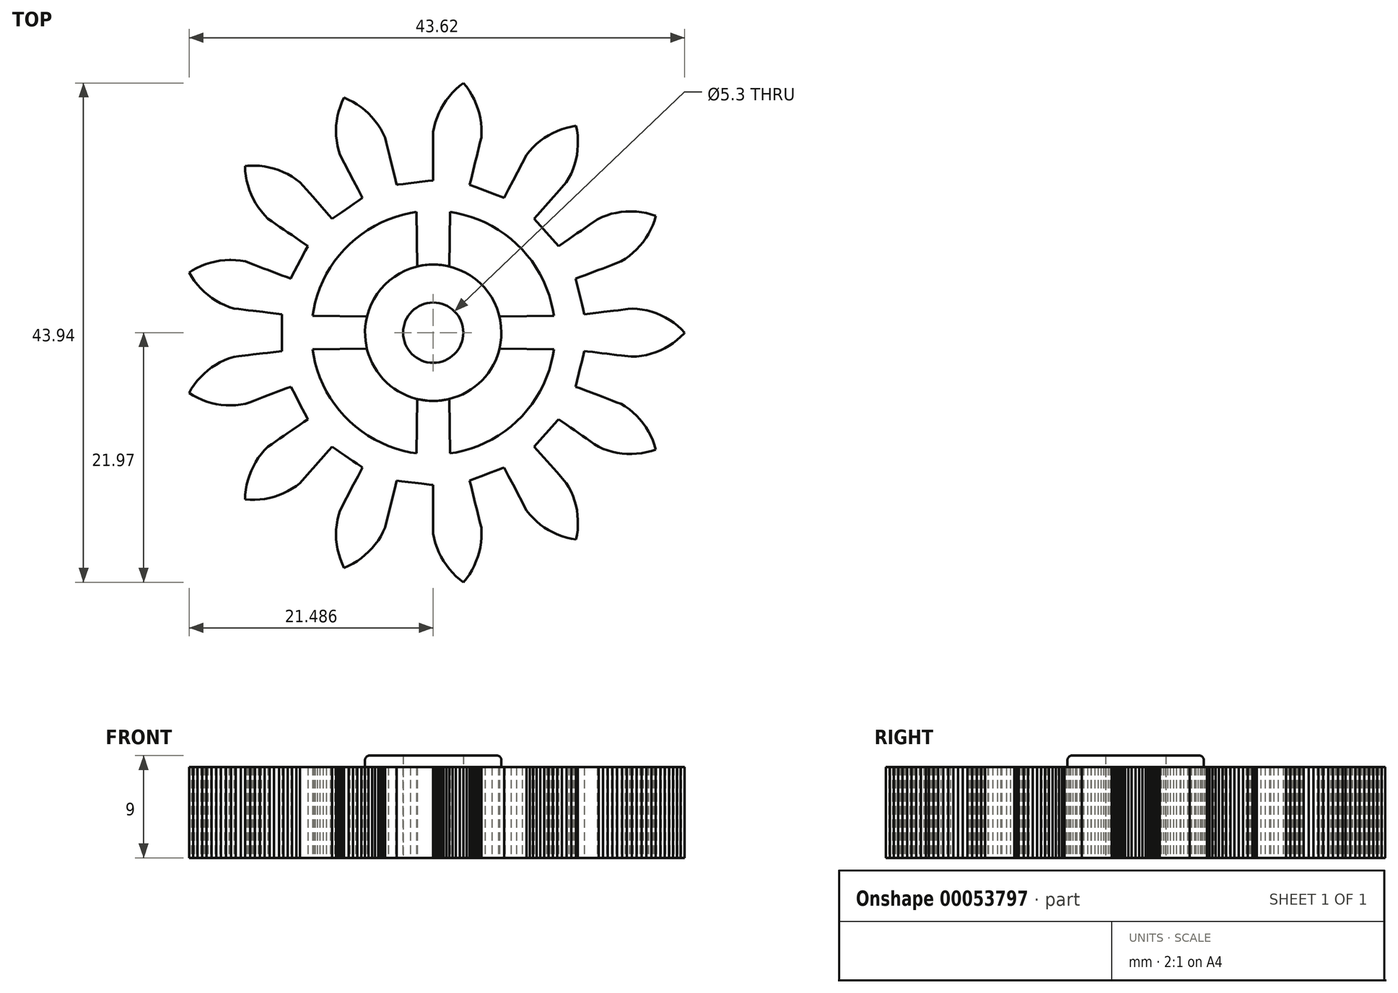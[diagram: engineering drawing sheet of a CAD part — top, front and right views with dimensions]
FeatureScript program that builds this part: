
annotation { "Feature Type Name" : "Feature", "Feature Type Description" : "" }
export const myFeature = defineFeature(function(context is Context, id is Id, definition is map)
    precondition{}
    {
        {
            var Q0;
            Q0=qCreatedBy(makeId("Top.planeOp"),FACE);
            var sketch = newSketch(context, id + "F0", { "sketchPlane" : qUnion([Q0])});
            skLineSegment(sketch, "E0", {"start": v(10.41, -1.62) * mm, "end": v(10.7, -1.65) * mm});
            skLineSegment(sketch, "E1", {"start": v(10.7, -1.65) * mm, "end": v(11.12, -1.7) * mm});
            skLineSegment(sketch, "E2", {"start": v(11.12, -1.7) * mm, "end": v(11.54, -1.75) * mm});
            skLineSegment(sketch, "E3", {"start": v(11.54, -1.75) * mm, "end": v(11.97, -1.8) * mm});
            skLineSegment(sketch, "E4", {"start": v(11.97, -1.8) * mm, "end": v(12.4, -1.86) * mm});
            skLineSegment(sketch, "E5", {"start": v(12.4, -1.86) * mm, "end": v(12.82, -1.9) * mm});
            skLineSegment(sketch, "E6", {"start": v(12.82, -1.9) * mm, "end": v(13.24, -1.96) * mm});
            skLineSegment(sketch, "E7", {"start": v(13.24, -1.96) * mm, "end": v(13.67, -2.01) * mm});
            skLineSegment(sketch, "E8", {"start": v(13.67, -2.01) * mm, "end": v(14.09, -2.06) * mm});
            skLineSegment(sketch, "E9", {"start": v(14.09, -2.06) * mm, "end": v(14.51, -2.11) * mm});
            skLineSegment(sketch, "E10", {"start": v(14.51, -2.11) * mm, "end": v(15, -2.1) * mm});
            skLineSegment(sketch, "E11", {"start": v(15, -2.1) * mm, "end": v(15.44, -2.05) * mm});
            skLineSegment(sketch, "E12", {"start": v(15.44, -2.05) * mm, "end": v(15.85, -1.97) * mm});
            skLineSegment(sketch, "E13", {"start": v(15.85, -1.97) * mm, "end": v(16.28, -1.86) * mm});
            skLineSegment(sketch, "E14", {"start": v(16.28, -1.86) * mm, "end": v(16.68, -1.72) * mm});
            skLineSegment(sketch, "E15", {"start": v(16.68, -1.72) * mm, "end": v(17.09, -1.55) * mm});
            skLineSegment(sketch, "E16", {"start": v(17.09, -1.55) * mm, "end": v(17.47, -1.37) * mm});
            skLineSegment(sketch, "E17", {"start": v(17.47, -1.37) * mm, "end": v(17.85, -1.15) * mm});
            skLineSegment(sketch, "E18", {"start": v(17.85, -1.15) * mm, "end": v(18.2, -0.92) * mm});
            skLineSegment(sketch, "E19", {"start": v(18.2, -0.92) * mm, "end": v(18.55, -0.64) * mm});
            skLineSegment(sketch, "E20", {"start": v(18.55, -0.64) * mm, "end": v(18.87, -0.37) * mm});
            skLineSegment(sketch, "E21", {"start": v(18.87, -0.37) * mm, "end": v(19.18, -0.05) * mm});
            skLineSegment(sketch, "E22", {"start": v(19.18, -0.05) * mm, "end": v(19.24, 0) * mm});
            skLineSegment(sketch, "E23", {"start": v(19.24, 0) * mm, "end": v(18.92, 0.31) * mm});
            skLineSegment(sketch, "E24", {"start": v(18.92, 0.31) * mm, "end": v(18.61, 0.6) * mm});
            skLineSegment(sketch, "E25", {"start": v(18.61, 0.6) * mm, "end": v(18.26, 0.87) * mm});
            skLineSegment(sketch, "E26", {"start": v(18.26, 0.87) * mm, "end": v(17.92, 1.1) * mm});
            skLineSegment(sketch, "E27", {"start": v(17.92, 1.1) * mm, "end": v(17.53, 1.33) * mm});
            skLineSegment(sketch, "E28", {"start": v(17.53, 1.33) * mm, "end": v(17.16, 1.52) * mm});
            skLineSegment(sketch, "E29", {"start": v(17.16, 1.52) * mm, "end": v(16.75, 1.7) * mm});
            skLineSegment(sketch, "E30", {"start": v(16.75, 1.7) * mm, "end": v(16.35, 1.84) * mm});
            skLineSegment(sketch, "E31", {"start": v(16.35, 1.84) * mm, "end": v(15.93, 1.95) * mm});
            skLineSegment(sketch, "E32", {"start": v(15.93, 1.95) * mm, "end": v(15.51, 2.04) * mm});
            skLineSegment(sketch, "E33", {"start": v(15.51, 2.04) * mm, "end": v(15.07, 2.1) * mm});
            skLineSegment(sketch, "E34", {"start": v(15.07, 2.1) * mm, "end": v(14.65, 2.13) * mm});
            skLineSegment(sketch, "E35", {"start": v(14.65, 2.13) * mm, "end": v(14.23, 2.08) * mm});
            skLineSegment(sketch, "E36", {"start": v(14.23, 2.08) * mm, "end": v(13.8, 2.03) * mm});
            skLineSegment(sketch, "E37", {"start": v(13.8, 2.03) * mm, "end": v(13.38, 1.98) * mm});
            skLineSegment(sketch, "E38", {"start": v(13.38, 1.98) * mm, "end": v(12.96, 1.92) * mm});
            skLineSegment(sketch, "E39", {"start": v(12.96, 1.92) * mm, "end": v(12.53, 1.87) * mm});
            skLineSegment(sketch, "E40", {"start": v(12.53, 1.87) * mm, "end": v(12.11, 1.82) * mm});
            skLineSegment(sketch, "E41", {"start": v(12.11, 1.82) * mm, "end": v(11.69, 1.77) * mm});
            skLineSegment(sketch, "E42", {"start": v(11.69, 1.77) * mm, "end": v(11.26, 1.72) * mm});
            skLineSegment(sketch, "E43", {"start": v(11.26, 1.72) * mm, "end": v(10.84, 1.67) * mm});
            skLineSegment(sketch, "E44", {"start": v(10.84, 1.67) * mm, "end": v(10.41, 1.62) * mm});
            skLineSegment(sketch, "E45", {"start": v(10.41, 1.62) * mm, "end": v(10.3, 2.05) * mm});
            skLineSegment(sketch, "E46", {"start": v(10.3, 2.05) * mm, "end": v(10.2, 2.48) * mm});
            skLineSegment(sketch, "E47", {"start": v(10.2, 2.48) * mm, "end": v(10.1, 2.9) * mm});
            skLineSegment(sketch, "E48", {"start": v(10.1, 2.9) * mm, "end": v(9.99, 3.34) * mm});
            skLineSegment(sketch, "E49", {"start": v(9.99, 3.34) * mm, "end": v(9.88, 3.77) * mm});
            skLineSegment(sketch, "E50", {"start": v(9.88, 3.77) * mm, "end": v(9.78, 4.2) * mm});
            skLineSegment(sketch, "E51", {"start": v(9.78, 4.2) * mm, "end": v(9.67, 4.63) * mm});
            skLineSegment(sketch, "E52", {"start": v(9.67, 4.63) * mm, "end": v(9.64, 4.75) * mm});
            skLineSegment(sketch, "E53", {"start": v(9.64, 4.75) * mm, "end": v(10.04, 4.9) * mm});
            skLineSegment(sketch, "E54", {"start": v(10.04, 4.9) * mm, "end": v(10.44, 5.06) * mm});
            skLineSegment(sketch, "E55", {"start": v(10.44, 5.06) * mm, "end": v(10.84, 5.2) * mm});
            skLineSegment(sketch, "E56", {"start": v(10.84, 5.2) * mm, "end": v(11.24, 5.36) * mm});
            skLineSegment(sketch, "E57", {"start": v(11.24, 5.36) * mm, "end": v(11.64, 5.51) * mm});
            skLineSegment(sketch, "E58", {"start": v(11.64, 5.51) * mm, "end": v(12.04, 5.66) * mm});
            skLineSegment(sketch, "E59", {"start": v(12.04, 5.66) * mm, "end": v(12.44, 5.81) * mm});
            skLineSegment(sketch, "E60", {"start": v(12.44, 5.81) * mm, "end": v(12.84, 5.97) * mm});
            skLineSegment(sketch, "E61", {"start": v(12.84, 5.97) * mm, "end": v(13.24, 6.12) * mm});
            skLineSegment(sketch, "E62", {"start": v(13.24, 6.12) * mm, "end": v(13.63, 6.27) * mm});
            skLineSegment(sketch, "E63", {"start": v(13.63, 6.27) * mm, "end": v(14, 6.5) * mm});
            skLineSegment(sketch, "E64", {"start": v(14, 6.5) * mm, "end": v(14.35, 6.75) * mm});
            skLineSegment(sketch, "E65", {"start": v(14.35, 6.75) * mm, "end": v(14.7, 7.03) * mm});
            skLineSegment(sketch, "E66", {"start": v(14.7, 7.03) * mm, "end": v(15, 7.32) * mm});
            skLineSegment(sketch, "E67", {"start": v(15, 7.32) * mm, "end": v(15.3, 7.64) * mm});
            skLineSegment(sketch, "E68", {"start": v(15.3, 7.64) * mm, "end": v(15.57, 7.97) * mm});
            skLineSegment(sketch, "E69", {"start": v(15.57, 7.97) * mm, "end": v(15.82, 8.33) * mm});
            skLineSegment(sketch, "E70", {"start": v(15.82, 8.33) * mm, "end": v(16.05, 8.69) * mm});
            skLineSegment(sketch, "E71", {"start": v(16.05, 8.69) * mm, "end": v(16.25, 9.08) * mm});
            skLineSegment(sketch, "E72", {"start": v(16.25, 9.08) * mm, "end": v(16.43, 9.46) * mm});
            skLineSegment(sketch, "E73", {"start": v(16.43, 9.46) * mm, "end": v(16.58, 9.88) * mm});
            skLineSegment(sketch, "E74", {"start": v(16.58, 9.88) * mm, "end": v(16.7, 10.28) * mm});
            skLineSegment(sketch, "E75", {"start": v(16.7, 10.28) * mm, "end": v(16.28, 10.42) * mm});
            skLineSegment(sketch, "E76", {"start": v(16.28, 10.42) * mm, "end": v(15.87, 10.52) * mm});
            skLineSegment(sketch, "E77", {"start": v(15.87, 10.52) * mm, "end": v(15.43, 10.6) * mm});
            skLineSegment(sketch, "E78", {"start": v(15.43, 10.6) * mm, "end": v(15.02, 10.65) * mm});
            skLineSegment(sketch, "E79", {"start": v(15.02, 10.65) * mm, "end": v(14.57, 10.67) * mm});
            skLineSegment(sketch, "E80", {"start": v(14.57, 10.67) * mm, "end": v(14.5, 10.68) * mm});
            skLineSegment(sketch, "E81", {"start": v(14.5, 10.68) * mm, "end": v(14.06, 10.66) * mm});
            skLineSegment(sketch, "E82", {"start": v(14.06, 10.66) * mm, "end": v(13.64, 10.62) * mm});
            skLineSegment(sketch, "E83", {"start": v(13.64, 10.62) * mm, "end": v(13.2, 10.55) * mm});
            skLineSegment(sketch, "E84", {"start": v(13.2, 10.55) * mm, "end": v(12.79, 10.46) * mm});
            skLineSegment(sketch, "E85", {"start": v(12.79, 10.46) * mm, "end": v(12.37, 10.33) * mm});
            skLineSegment(sketch, "E86", {"start": v(12.37, 10.33) * mm, "end": v(11.97, 10.18) * mm});
            skLineSegment(sketch, "E87", {"start": v(11.97, 10.18) * mm, "end": v(11.54, 9.96) * mm});
            skLineSegment(sketch, "E88", {"start": v(11.54, 9.96) * mm, "end": v(11.19, 9.72) * mm});
            skLineSegment(sketch, "E89", {"start": v(11.19, 9.72) * mm, "end": v(10.83, 9.48) * mm});
            skLineSegment(sketch, "E90", {"start": v(10.83, 9.48) * mm, "end": v(10.48, 9.23) * mm});
            skLineSegment(sketch, "E91", {"start": v(10.48, 9.23) * mm, "end": v(10.13, 9) * mm});
            skLineSegment(sketch, "E92", {"start": v(10.13, 9) * mm, "end": v(9.78, 8.75) * mm});
            skLineSegment(sketch, "E93", {"start": v(9.78, 8.75) * mm, "end": v(9.43, 8.5) * mm});
            skLineSegment(sketch, "E94", {"start": v(9.43, 8.5) * mm, "end": v(9.08, 8.26) * mm});
            skLineSegment(sketch, "E95", {"start": v(9.08, 8.26) * mm, "end": v(8.72, 8.02) * mm});
            skLineSegment(sketch, "E96", {"start": v(8.72, 8.02) * mm, "end": v(8.37, 7.78) * mm});
            skLineSegment(sketch, "E97", {"start": v(8.37, 7.78) * mm, "end": v(8.14, 7.62) * mm});
            skLineSegment(sketch, "E98", {"start": v(8.14, 7.62) * mm, "end": v(7.84, 7.95) * mm});
            skLineSegment(sketch, "E99", {"start": v(7.84, 7.95) * mm, "end": v(7.55, 8.28) * mm});
            skLineSegment(sketch, "E100", {"start": v(7.55, 8.28) * mm, "end": v(7.26, 8.6) * mm});
            skLineSegment(sketch, "E101", {"start": v(7.26, 8.6) * mm, "end": v(6.96, 8.94) * mm});
            skLineSegment(sketch, "E102", {"start": v(6.96, 8.94) * mm, "end": v(6.67, 9.27) * mm});
            skLineSegment(sketch, "E103", {"start": v(6.67, 9.27) * mm, "end": v(6.38, 9.6) * mm});
            skLineSegment(sketch, "E104", {"start": v(6.38, 9.6) * mm, "end": v(6.08, 9.94) * mm});
            skLineSegment(sketch, "E105", {"start": v(6.08, 9.94) * mm, "end": v(6, 10.03) * mm});
            skLineSegment(sketch, "E106", {"start": v(6, 10.03) * mm, "end": v(6.28, 10.35) * mm});
            skLineSegment(sketch, "E107", {"start": v(6.28, 10.35) * mm, "end": v(6.56, 10.67) * mm});
            skLineSegment(sketch, "E108", {"start": v(6.56, 10.67) * mm, "end": v(6.85, 11) * mm});
            skLineSegment(sketch, "E109", {"start": v(6.85, 11) * mm, "end": v(7.13, 11.31) * mm});
            skLineSegment(sketch, "E110", {"start": v(7.13, 11.31) * mm, "end": v(7.41, 11.63) * mm});
            skLineSegment(sketch, "E111", {"start": v(7.41, 11.63) * mm, "end": v(7.7, 11.95) * mm});
            skLineSegment(sketch, "E112", {"start": v(7.7, 11.95) * mm, "end": v(7.98, 12.27) * mm});
            skLineSegment(sketch, "E113", {"start": v(7.98, 12.27) * mm, "end": v(8.26, 12.6) * mm});
            skLineSegment(sketch, "E114", {"start": v(8.26, 12.6) * mm, "end": v(8.55, 12.91) * mm});
            skLineSegment(sketch, "E115", {"start": v(8.55, 12.91) * mm, "end": v(8.83, 13.23) * mm});
            skLineSegment(sketch, "E116", {"start": v(8.83, 13.23) * mm, "end": v(9.05, 13.62) * mm});
            skLineSegment(sketch, "E117", {"start": v(9.05, 13.62) * mm, "end": v(9.24, 14) * mm});
            skLineSegment(sketch, "E118", {"start": v(9.24, 14) * mm, "end": v(9.41, 14.4) * mm});
            skLineSegment(sketch, "E119", {"start": v(9.41, 14.4) * mm, "end": v(9.55, 14.8) * mm});
            skLineSegment(sketch, "E120", {"start": v(9.55, 14.8) * mm, "end": v(9.66, 15.23) * mm});
            skLineSegment(sketch, "E121", {"start": v(9.66, 15.23) * mm, "end": v(9.75, 15.64) * mm});
            skLineSegment(sketch, "E122", {"start": v(9.75, 15.64) * mm, "end": v(9.8, 16.08) * mm});
            skLineSegment(sketch, "E123", {"start": v(9.8, 16.08) * mm, "end": v(9.84, 16.5) * mm});
            skLineSegment(sketch, "E124", {"start": v(9.84, 16.5) * mm, "end": v(9.84, 16.94) * mm});
            skLineSegment(sketch, "E125", {"start": v(9.84, 16.94) * mm, "end": v(9.82, 17.36) * mm});
            skLineSegment(sketch, "E126", {"start": v(9.82, 17.36) * mm, "end": v(9.76, 17.8) * mm});
            skLineSegment(sketch, "E127", {"start": v(9.76, 17.8) * mm, "end": v(9.68, 18.21) * mm});
            skLineSegment(sketch, "E128", {"start": v(9.68, 18.21) * mm, "end": v(9.24, 18.13) * mm});
            skLineSegment(sketch, "E129", {"start": v(9.24, 18.13) * mm, "end": v(8.83, 18.04) * mm});
            skLineSegment(sketch, "E130", {"start": v(8.83, 18.04) * mm, "end": v(8.4, 17.9) * mm});
            skLineSegment(sketch, "E131", {"start": v(8.4, 17.9) * mm, "end": v(8.01, 17.76) * mm});
            skLineSegment(sketch, "E132", {"start": v(8.01, 17.76) * mm, "end": v(7.61, 17.57) * mm});
            skLineSegment(sketch, "E133", {"start": v(7.61, 17.57) * mm, "end": v(7.24, 17.37) * mm});
            skLineSegment(sketch, "E134", {"start": v(7.24, 17.37) * mm, "end": v(6.87, 17.13) * mm});
            skLineSegment(sketch, "E135", {"start": v(6.87, 17.13) * mm, "end": v(6.53, 16.88) * mm});
            skLineSegment(sketch, "E136", {"start": v(6.53, 16.88) * mm, "end": v(6.2, 16.6) * mm});
            skLineSegment(sketch, "E137", {"start": v(6.2, 16.6) * mm, "end": v(5.88, 16.3) * mm});
            skLineSegment(sketch, "E138", {"start": v(5.88, 16.3) * mm, "end": v(5.59, 15.98) * mm});
            skLineSegment(sketch, "E139", {"start": v(5.59, 15.98) * mm, "end": v(5.32, 15.65) * mm});
            skLineSegment(sketch, "E140", {"start": v(5.32, 15.65) * mm, "end": v(5.12, 15.27) * mm});
            skLineSegment(sketch, "E141", {"start": v(5.12, 15.27) * mm, "end": v(4.92, 14.9) * mm});
            skLineSegment(sketch, "E142", {"start": v(4.92, 14.9) * mm, "end": v(4.73, 14.52) * mm});
            skLineSegment(sketch, "E143", {"start": v(4.73, 14.52) * mm, "end": v(4.53, 14.14) * mm});
            skLineSegment(sketch, "E144", {"start": v(4.53, 14.14) * mm, "end": v(4.33, 13.76) * mm});
            skLineSegment(sketch, "E145", {"start": v(4.33, 13.76) * mm, "end": v(4.13, 13.38) * mm});
            skLineSegment(sketch, "E146", {"start": v(4.13, 13.38) * mm, "end": v(3.93, 13) * mm});
            skLineSegment(sketch, "E147", {"start": v(3.93, 13) * mm, "end": v(3.73, 12.63) * mm});
            skLineSegment(sketch, "E148", {"start": v(3.73, 12.63) * mm, "end": v(3.53, 12.25) * mm});
            skLineSegment(sketch, "E149", {"start": v(3.53, 12.25) * mm, "end": v(3.34, 11.87) * mm});
            skLineSegment(sketch, "E150", {"start": v(3.34, 11.87) * mm, "end": v(2.92, 12.03) * mm});
            skLineSegment(sketch, "E151", {"start": v(2.92, 12.03) * mm, "end": v(2.5, 12.18) * mm});
            skLineSegment(sketch, "E152", {"start": v(2.5, 12.18) * mm, "end": v(2.1, 12.34) * mm});
            skLineSegment(sketch, "E153", {"start": v(2.1, 12.34) * mm, "end": v(1.68, 12.5) * mm});
            skLineSegment(sketch, "E154", {"start": v(1.68, 12.5) * mm, "end": v(1.26, 12.66) * mm});
            skLineSegment(sketch, "E155", {"start": v(1.26, 12.66) * mm, "end": v(0.85, 12.81) * mm});
            skLineSegment(sketch, "E156", {"start": v(0.85, 12.81) * mm, "end": v(0.44, 12.97) * mm});
            skLineSegment(sketch, "E157", {"start": v(0.44, 12.97) * mm, "end": v(0.31, 13.02) * mm});
            skLineSegment(sketch, "E158", {"start": v(0.31, 13.02) * mm, "end": v(0.42, 13.43) * mm});
            skLineSegment(sketch, "E159", {"start": v(0.42, 13.43) * mm, "end": v(0.52, 13.85) * mm});
            skLineSegment(sketch, "E160", {"start": v(0.52, 13.85) * mm, "end": v(0.62, 14.26) * mm});
            skLineSegment(sketch, "E161", {"start": v(0.62, 14.26) * mm, "end": v(0.72, 14.68) * mm});
            skLineSegment(sketch, "E162", {"start": v(0.72, 14.68) * mm, "end": v(0.83, 15.1) * mm});
            skLineSegment(sketch, "E163", {"start": v(0.83, 15.1) * mm, "end": v(0.93, 15.5) * mm});
            skLineSegment(sketch, "E164", {"start": v(0.93, 15.5) * mm, "end": v(1.03, 15.92) * mm});
            skLineSegment(sketch, "E165", {"start": v(1.03, 15.92) * mm, "end": v(1.13, 16.33) * mm});
            skLineSegment(sketch, "E166", {"start": v(1.13, 16.33) * mm, "end": v(1.23, 16.75) * mm});
            skLineSegment(sketch, "E167", {"start": v(1.23, 16.75) * mm, "end": v(1.34, 17.16) * mm});
            skLineSegment(sketch, "E168", {"start": v(1.34, 17.16) * mm, "end": v(1.35, 17.6) * mm});
            skLineSegment(sketch, "E169", {"start": v(1.35, 17.6) * mm, "end": v(1.35, 18.03) * mm});
            skLineSegment(sketch, "E170", {"start": v(1.35, 18.03) * mm, "end": v(1.3, 18.47) * mm});
            skLineSegment(sketch, "E171", {"start": v(1.3, 18.47) * mm, "end": v(1.25, 18.89) * mm});
            skLineSegment(sketch, "E172", {"start": v(1.25, 18.89) * mm, "end": v(1.15, 19.32) * mm});
            skLineSegment(sketch, "E173", {"start": v(1.15, 19.32) * mm, "end": v(1.04, 19.72) * mm});
            skLineSegment(sketch, "E174", {"start": v(1.04, 19.72) * mm, "end": v(0.88, 20.14) * mm});
            skLineSegment(sketch, "E175", {"start": v(0.88, 20.14) * mm, "end": v(0.72, 20.52) * mm});
            skLineSegment(sketch, "E176", {"start": v(0.72, 20.52) * mm, "end": v(0.5, 20.92) * mm});
            skLineSegment(sketch, "E177", {"start": v(0.5, 20.92) * mm, "end": v(0.3, 21.28) * mm});
            skLineSegment(sketch, "E178", {"start": v(0.3, 21.28) * mm, "end": v(0.04, 21.64) * mm});
            skLineSegment(sketch, "E179", {"start": v(0.04, 21.64) * mm, "end": v(-0.23, 21.97) * mm});
            skLineSegment(sketch, "E180", {"start": v(-0.23, 21.97) * mm, "end": v(-0.58, 21.7) * mm});
            skLineSegment(sketch, "E181", {"start": v(-0.58, 21.7) * mm, "end": v(-0.9, 21.42) * mm});
            skLineSegment(sketch, "E182", {"start": v(-0.9, 21.42) * mm, "end": v(-1.2, 21.1) * mm});
            skLineSegment(sketch, "E183", {"start": v(-1.2, 21.1) * mm, "end": v(-1.49, 20.8) * mm});
            skLineSegment(sketch, "E184", {"start": v(-1.49, 20.8) * mm, "end": v(-1.75, 20.44) * mm});
            skLineSegment(sketch, "E185", {"start": v(-1.75, 20.44) * mm, "end": v(-1.99, 20.1) * mm});
            skLineSegment(sketch, "E186", {"start": v(-1.99, 20.1) * mm, "end": v(-2.2, 19.7) * mm});
            skLineSegment(sketch, "E187", {"start": v(-2.2, 19.7) * mm, "end": v(-2.4, 19.33) * mm});
            skLineSegment(sketch, "E188", {"start": v(-2.4, 19.33) * mm, "end": v(-2.56, 18.92) * mm});
            skLineSegment(sketch, "E189", {"start": v(-2.56, 18.92) * mm, "end": v(-2.7, 18.52) * mm});
            skLineSegment(sketch, "E190", {"start": v(-2.7, 18.52) * mm, "end": v(-2.81, 18.1) * mm});
            skLineSegment(sketch, "E191", {"start": v(-2.81, 18.1) * mm, "end": v(-2.9, 17.68) * mm});
            skLineSegment(sketch, "E192", {"start": v(-2.9, 17.68) * mm, "end": v(-2.9, 17.25) * mm});
            skLineSegment(sketch, "E193", {"start": v(-2.9, 17.25) * mm, "end": v(-2.9, 16.82) * mm});
            skLineSegment(sketch, "E194", {"start": v(-2.9, 16.82) * mm, "end": v(-2.9, 16.4) * mm});
            skLineSegment(sketch, "E195", {"start": v(-2.9, 16.4) * mm, "end": v(-2.9, 15.97) * mm});
            skLineSegment(sketch, "E196", {"start": v(-2.9, 15.97) * mm, "end": v(-2.9, 15.54) * mm});
            skLineSegment(sketch, "E197", {"start": v(-2.9, 15.54) * mm, "end": v(-2.9, 15.11) * mm});
            skLineSegment(sketch, "E198", {"start": v(-2.9, 15.11) * mm, "end": v(-2.9, 14.69) * mm});
            skLineSegment(sketch, "E199", {"start": v(-2.9, 14.69) * mm, "end": v(-2.9, 14.26) * mm});
            skLineSegment(sketch, "E200", {"start": v(-2.9, 14.26) * mm, "end": v(-2.9, 13.83) * mm});
            skLineSegment(sketch, "E201", {"start": v(-2.9, 13.83) * mm, "end": v(-2.9, 13.4) * mm});
            skLineSegment(sketch, "E202", {"start": v(-2.9, 13.4) * mm, "end": v(-3.33, 13.35) * mm});
            skLineSegment(sketch, "E203", {"start": v(-3.33, 13.35) * mm, "end": v(-3.77, 13.3) * mm});
            skLineSegment(sketch, "E204", {"start": v(-3.77, 13.3) * mm, "end": v(-4.21, 13.25) * mm});
            skLineSegment(sketch, "E205", {"start": v(-4.21, 13.25) * mm, "end": v(-4.65, 13.2) * mm});
            skLineSegment(sketch, "E206", {"start": v(-4.65, 13.2) * mm, "end": v(-5.1, 13.14) * mm});
            skLineSegment(sketch, "E207", {"start": v(-5.1, 13.14) * mm, "end": v(-5.53, 13.09) * mm});
            skLineSegment(sketch, "E208", {"start": v(-5.53, 13.09) * mm, "end": v(-5.97, 13.03) * mm});
            skLineSegment(sketch, "E209", {"start": v(-5.97, 13.03) * mm, "end": v(-6.1, 13.02) * mm});
            skLineSegment(sketch, "E210", {"start": v(-6.1, 13.02) * mm, "end": v(-6.2, 13.43) * mm});
            skLineSegment(sketch, "E211", {"start": v(-6.2, 13.43) * mm, "end": v(-6.3, 13.85) * mm});
            skLineSegment(sketch, "E212", {"start": v(-6.3, 13.85) * mm, "end": v(-6.4, 14.26) * mm});
            skLineSegment(sketch, "E213", {"start": v(-6.4, 14.26) * mm, "end": v(-6.51, 14.68) * mm});
            skLineSegment(sketch, "E214", {"start": v(-6.51, 14.68) * mm, "end": v(-6.61, 15.1) * mm});
            skLineSegment(sketch, "E215", {"start": v(-6.61, 15.1) * mm, "end": v(-6.72, 15.5) * mm});
            skLineSegment(sketch, "E216", {"start": v(-6.72, 15.5) * mm, "end": v(-6.82, 15.92) * mm});
            skLineSegment(sketch, "E217", {"start": v(-6.82, 15.92) * mm, "end": v(-6.92, 16.33) * mm});
            skLineSegment(sketch, "E218", {"start": v(-6.92, 16.33) * mm, "end": v(-7.02, 16.75) * mm});
            skLineSegment(sketch, "E219", {"start": v(-7.02, 16.75) * mm, "end": v(-7.12, 17.16) * mm});
            skLineSegment(sketch, "E220", {"start": v(-7.12, 17.16) * mm, "end": v(-7.31, 17.56) * mm});
            skLineSegment(sketch, "E221", {"start": v(-7.31, 17.56) * mm, "end": v(-7.51, 17.93) * mm});
            skLineSegment(sketch, "E222", {"start": v(-7.51, 17.93) * mm, "end": v(-7.76, 18.3) * mm});
            skLineSegment(sketch, "E223", {"start": v(-7.76, 18.3) * mm, "end": v(-8, 18.65) * mm});
            skLineSegment(sketch, "E224", {"start": v(-8, 18.65) * mm, "end": v(-8.29, 18.98) * mm});
            skLineSegment(sketch, "E225", {"start": v(-8.29, 18.98) * mm, "end": v(-8.58, 19.29) * mm});
            skLineSegment(sketch, "E226", {"start": v(-8.58, 19.29) * mm, "end": v(-8.9, 19.59) * mm});
            skLineSegment(sketch, "E227", {"start": v(-8.9, 19.59) * mm, "end": v(-9.24, 19.85) * mm});
            skLineSegment(sketch, "E228", {"start": v(-9.24, 19.85) * mm, "end": v(-9.6, 20.1) * mm});
            skLineSegment(sketch, "E229", {"start": v(-9.6, 20.1) * mm, "end": v(-9.96, 20.32) * mm});
            skLineSegment(sketch, "E230", {"start": v(-9.96, 20.32) * mm, "end": v(-10.36, 20.52) * mm});
            skLineSegment(sketch, "E231", {"start": v(-10.36, 20.52) * mm, "end": v(-10.74, 20.7) * mm});
            skLineSegment(sketch, "E232", {"start": v(-10.74, 20.7) * mm, "end": v(-10.93, 20.29) * mm});
            skLineSegment(sketch, "E233", {"start": v(-10.93, 20.29) * mm, "end": v(-11.08, 19.9) * mm});
            skLineSegment(sketch, "E234", {"start": v(-11.08, 19.9) * mm, "end": v(-11.2, 19.47) * mm});
            skLineSegment(sketch, "E235", {"start": v(-11.2, 19.47) * mm, "end": v(-11.31, 19.06) * mm});
            skLineSegment(sketch, "E236", {"start": v(-11.31, 19.06) * mm, "end": v(-11.38, 18.63) * mm});
            skLineSegment(sketch, "E237", {"start": v(-11.38, 18.63) * mm, "end": v(-11.43, 18.2) * mm});
            skLineSegment(sketch, "E238", {"start": v(-11.43, 18.2) * mm, "end": v(-11.44, 17.77) * mm});
            skLineSegment(sketch, "E239", {"start": v(-11.44, 17.77) * mm, "end": v(-11.44, 17.35) * mm});
            skLineSegment(sketch, "E240", {"start": v(-11.44, 17.35) * mm, "end": v(-11.4, 16.9) * mm});
            skLineSegment(sketch, "E241", {"start": v(-11.4, 16.9) * mm, "end": v(-11.33, 16.49) * mm});
            skLineSegment(sketch, "E242", {"start": v(-11.33, 16.49) * mm, "end": v(-11.23, 16.06) * mm});
            skLineSegment(sketch, "E243", {"start": v(-11.23, 16.06) * mm, "end": v(-11.1, 15.65) * mm});
            skLineSegment(sketch, "E244", {"start": v(-11.1, 15.65) * mm, "end": v(-10.91, 15.27) * mm});
            skLineSegment(sketch, "E245", {"start": v(-10.91, 15.27) * mm, "end": v(-10.71, 14.9) * mm});
            skLineSegment(sketch, "E246", {"start": v(-10.71, 14.9) * mm, "end": v(-10.51, 14.52) * mm});
            skLineSegment(sketch, "E247", {"start": v(-10.51, 14.52) * mm, "end": v(-10.32, 14.14) * mm});
            skLineSegment(sketch, "E248", {"start": v(-10.32, 14.14) * mm, "end": v(-10.12, 13.76) * mm});
            skLineSegment(sketch, "E249", {"start": v(-10.12, 13.76) * mm, "end": v(-9.92, 13.38) * mm});
            skLineSegment(sketch, "E250", {"start": v(-9.92, 13.38) * mm, "end": v(-9.72, 13) * mm});
            skLineSegment(sketch, "E251", {"start": v(-9.72, 13) * mm, "end": v(-9.52, 12.63) * mm});
            skLineSegment(sketch, "E252", {"start": v(-9.52, 12.63) * mm, "end": v(-9.32, 12.25) * mm});
            skLineSegment(sketch, "E253", {"start": v(-9.32, 12.25) * mm, "end": v(-9.12, 11.87) * mm});
            skLineSegment(sketch, "E254", {"start": v(-9.12, 11.87) * mm, "end": v(-9.49, 11.62) * mm});
            skLineSegment(sketch, "E255", {"start": v(-9.49, 11.62) * mm, "end": v(-9.85, 11.37) * mm});
            skLineSegment(sketch, "E256", {"start": v(-9.85, 11.37) * mm, "end": v(-10.22, 11.12) * mm});
            skLineSegment(sketch, "E257", {"start": v(-10.22, 11.12) * mm, "end": v(-10.58, 10.86) * mm});
            skLineSegment(sketch, "E258", {"start": v(-10.58, 10.86) * mm, "end": v(-10.95, 10.61) * mm});
            skLineSegment(sketch, "E259", {"start": v(-10.95, 10.61) * mm, "end": v(-11.31, 10.36) * mm});
            skLineSegment(sketch, "E260", {"start": v(-11.31, 10.36) * mm, "end": v(-11.68, 10.1) * mm});
            skLineSegment(sketch, "E261", {"start": v(-11.68, 10.1) * mm, "end": v(-11.78, 10.03) * mm});
            skLineSegment(sketch, "E262", {"start": v(-11.78, 10.03) * mm, "end": v(-12.07, 10.35) * mm});
            skLineSegment(sketch, "E263", {"start": v(-12.07, 10.35) * mm, "end": v(-12.35, 10.67) * mm});
            skLineSegment(sketch, "E264", {"start": v(-12.35, 10.67) * mm, "end": v(-12.63, 11) * mm});
            skLineSegment(sketch, "E265", {"start": v(-12.63, 11) * mm, "end": v(-12.92, 11.31) * mm});
            skLineSegment(sketch, "E266", {"start": v(-12.92, 11.31) * mm, "end": v(-13.2, 11.63) * mm});
            skLineSegment(sketch, "E267", {"start": v(-13.2, 11.63) * mm, "end": v(-13.48, 11.95) * mm});
            skLineSegment(sketch, "E268", {"start": v(-13.48, 11.95) * mm, "end": v(-13.77, 12.27) * mm});
            skLineSegment(sketch, "E269", {"start": v(-13.77, 12.27) * mm, "end": v(-14.05, 12.6) * mm});
            skLineSegment(sketch, "E270", {"start": v(-14.05, 12.6) * mm, "end": v(-14.33, 12.91) * mm});
            skLineSegment(sketch, "E271", {"start": v(-14.33, 12.91) * mm, "end": v(-14.62, 13.23) * mm});
            skLineSegment(sketch, "E272", {"start": v(-14.62, 13.23) * mm, "end": v(-14.97, 13.5) * mm});
            skLineSegment(sketch, "E273", {"start": v(-14.97, 13.5) * mm, "end": v(-15.32, 13.73) * mm});
            skLineSegment(sketch, "E274", {"start": v(-15.32, 13.73) * mm, "end": v(-15.7, 13.95) * mm});
            skLineSegment(sketch, "E275", {"start": v(-15.7, 13.95) * mm, "end": v(-16.08, 14.14) * mm});
            skLineSegment(sketch, "E276", {"start": v(-16.08, 14.14) * mm, "end": v(-16.5, 14.3) * mm});
            skLineSegment(sketch, "E277", {"start": v(-16.5, 14.3) * mm, "end": v(-16.9, 14.44) * mm});
            skLineSegment(sketch, "E278", {"start": v(-16.9, 14.44) * mm, "end": v(-17.32, 14.55) * mm});
            skLineSegment(sketch, "E279", {"start": v(-17.32, 14.55) * mm, "end": v(-17.74, 14.63) * mm});
            skLineSegment(sketch, "E280", {"start": v(-17.74, 14.63) * mm, "end": v(-18.18, 14.68) * mm});
            skLineSegment(sketch, "E281", {"start": v(-18.18, 14.68) * mm, "end": v(-18.6, 14.7) * mm});
            skLineSegment(sketch, "E282", {"start": v(-18.6, 14.7) * mm, "end": v(-18.77, 14.71) * mm});
            skLineSegment(sketch, "E283", {"start": v(-18.77, 14.71) * mm, "end": v(-19.21, 14.7) * mm});
            skLineSegment(sketch, "E284", {"start": v(-19.21, 14.7) * mm, "end": v(-19.46, 14.67) * mm});
            skLineSegment(sketch, "E285", {"start": v(-19.46, 14.67) * mm, "end": v(-19.43, 14.23) * mm});
            skLineSegment(sketch, "E286", {"start": v(-19.43, 14.23) * mm, "end": v(-19.39, 13.81) * mm});
            skLineSegment(sketch, "E287", {"start": v(-19.39, 13.81) * mm, "end": v(-19.3, 13.38) * mm});
            skLineSegment(sketch, "E288", {"start": v(-19.3, 13.38) * mm, "end": v(-19.2, 12.97) * mm});
            skLineSegment(sketch, "E289", {"start": v(-19.2, 12.97) * mm, "end": v(-19.07, 12.55) * mm});
            skLineSegment(sketch, "E290", {"start": v(-19.07, 12.55) * mm, "end": v(-18.91, 12.16) * mm});
            skLineSegment(sketch, "E291", {"start": v(-18.91, 12.16) * mm, "end": v(-18.72, 11.76) * mm});
            skLineSegment(sketch, "E292", {"start": v(-18.72, 11.76) * mm, "end": v(-18.52, 11.39) * mm});
            skLineSegment(sketch, "E293", {"start": v(-18.52, 11.39) * mm, "end": v(-18.27, 11.02) * mm});
            skLineSegment(sketch, "E294", {"start": v(-18.27, 11.02) * mm, "end": v(-18.02, 10.68) * mm});
            skLineSegment(sketch, "E295", {"start": v(-18.02, 10.68) * mm, "end": v(-17.73, 10.35) * mm});
            skLineSegment(sketch, "E296", {"start": v(-17.73, 10.35) * mm, "end": v(-17.44, 10.04) * mm});
            skLineSegment(sketch, "E297", {"start": v(-17.44, 10.04) * mm, "end": v(-17.1, 9.8) * mm});
            skLineSegment(sketch, "E298", {"start": v(-17.1, 9.8) * mm, "end": v(-16.74, 9.56) * mm});
            skLineSegment(sketch, "E299", {"start": v(-16.74, 9.56) * mm, "end": v(-16.39, 9.31) * mm});
            skLineSegment(sketch, "E300", {"start": v(-16.39, 9.31) * mm, "end": v(-16.04, 9.07) * mm});
            skLineSegment(sketch, "E301", {"start": v(-16.04, 9.07) * mm, "end": v(-15.68, 8.83) * mm});
            skLineSegment(sketch, "E302", {"start": v(-15.68, 8.83) * mm, "end": v(-15.33, 8.59) * mm});
            skLineSegment(sketch, "E303", {"start": v(-15.33, 8.59) * mm, "end": v(-14.98, 8.34) * mm});
            skLineSegment(sketch, "E304", {"start": v(-14.98, 8.34) * mm, "end": v(-14.63, 8.1) * mm});
            skLineSegment(sketch, "E305", {"start": v(-14.63, 8.1) * mm, "end": v(-14.28, 7.86) * mm});
            skLineSegment(sketch, "E306", {"start": v(-14.28, 7.86) * mm, "end": v(-13.93, 7.62) * mm});
            skLineSegment(sketch, "E307", {"start": v(-13.93, 7.62) * mm, "end": v(-14.13, 7.22) * mm});
            skLineSegment(sketch, "E308", {"start": v(-14.13, 7.22) * mm, "end": v(-14.34, 6.83) * mm});
            skLineSegment(sketch, "E309", {"start": v(-14.34, 6.83) * mm, "end": v(-14.54, 6.44) * mm});
            skLineSegment(sketch, "E310", {"start": v(-14.54, 6.44) * mm, "end": v(-14.75, 6.05) * mm});
            skLineSegment(sketch, "E311", {"start": v(-14.75, 6.05) * mm, "end": v(-14.96, 5.65) * mm});
            skLineSegment(sketch, "E312", {"start": v(-14.96, 5.65) * mm, "end": v(-15.16, 5.26) * mm});
            skLineSegment(sketch, "E313", {"start": v(-15.16, 5.26) * mm, "end": v(-15.37, 4.87) * mm});
            skLineSegment(sketch, "E314", {"start": v(-15.37, 4.87) * mm, "end": v(-15.43, 4.75) * mm});
            skLineSegment(sketch, "E315", {"start": v(-15.43, 4.75) * mm, "end": v(-15.83, 4.9) * mm});
            skLineSegment(sketch, "E316", {"start": v(-15.83, 4.9) * mm, "end": v(-16.23, 5.06) * mm});
            skLineSegment(sketch, "E317", {"start": v(-16.23, 5.06) * mm, "end": v(-16.63, 5.2) * mm});
            skLineSegment(sketch, "E318", {"start": v(-16.63, 5.2) * mm, "end": v(-17.03, 5.36) * mm});
            skLineSegment(sketch, "E319", {"start": v(-17.03, 5.36) * mm, "end": v(-17.43, 5.51) * mm});
            skLineSegment(sketch, "E320", {"start": v(-17.43, 5.51) * mm, "end": v(-17.83, 5.66) * mm});
            skLineSegment(sketch, "E321", {"start": v(-17.83, 5.66) * mm, "end": v(-18.22, 5.81) * mm});
            skLineSegment(sketch, "E322", {"start": v(-18.22, 5.81) * mm, "end": v(-18.62, 5.97) * mm});
            skLineSegment(sketch, "E323", {"start": v(-18.62, 5.97) * mm, "end": v(-19.02, 6.12) * mm});
            skLineSegment(sketch, "E324", {"start": v(-19.02, 6.12) * mm, "end": v(-19.42, 6.27) * mm});
            skLineSegment(sketch, "E325", {"start": v(-19.42, 6.27) * mm, "end": v(-19.86, 6.34) * mm});
            skLineSegment(sketch, "E326", {"start": v(-19.86, 6.34) * mm, "end": v(-20.28, 6.39) * mm});
            skLineSegment(sketch, "E327", {"start": v(-20.28, 6.39) * mm, "end": v(-20.72, 6.4) * mm});
            skLineSegment(sketch, "E328", {"start": v(-20.72, 6.4) * mm, "end": v(-20.8, 6.4) * mm});
            skLineSegment(sketch, "E329", {"start": v(-20.8, 6.4) * mm, "end": v(-21.24, 6.38) * mm});
            skLineSegment(sketch, "E330", {"start": v(-21.24, 6.38) * mm, "end": v(-21.66, 6.34) * mm});
            skLineSegment(sketch, "E331", {"start": v(-21.66, 6.34) * mm, "end": v(-22.1, 6.26) * mm});
            skLineSegment(sketch, "E332", {"start": v(-22.1, 6.26) * mm, "end": v(-22.5, 6.16) * mm});
            skLineSegment(sketch, "E333", {"start": v(-22.5, 6.16) * mm, "end": v(-22.93, 6.02) * mm});
            skLineSegment(sketch, "E334", {"start": v(-22.93, 6.02) * mm, "end": v(-23.32, 5.87) * mm});
            skLineSegment(sketch, "E335", {"start": v(-23.32, 5.87) * mm, "end": v(-23.72, 5.68) * mm});
            skLineSegment(sketch, "E336", {"start": v(-23.72, 5.68) * mm, "end": v(-24.09, 5.48) * mm});
            skLineSegment(sketch, "E337", {"start": v(-24.09, 5.48) * mm, "end": v(-24.38, 5.3) * mm});
            skLineSegment(sketch, "E338", {"start": v(-24.38, 5.3) * mm, "end": v(-24.15, 4.92) * mm});
            skLineSegment(sketch, "E339", {"start": v(-24.15, 4.92) * mm, "end": v(-23.92, 4.57) * mm});
            skLineSegment(sketch, "E340", {"start": v(-23.92, 4.57) * mm, "end": v(-23.64, 4.22) * mm});
            skLineSegment(sketch, "E341", {"start": v(-23.64, 4.22) * mm, "end": v(-23.36, 3.9) * mm});
            skLineSegment(sketch, "E342", {"start": v(-23.36, 3.9) * mm, "end": v(-23.05, 3.6) * mm});
            skLineSegment(sketch, "E343", {"start": v(-23.05, 3.6) * mm, "end": v(-22.73, 3.32) * mm});
            skLineSegment(sketch, "E344", {"start": v(-22.73, 3.32) * mm, "end": v(-22.37, 3.06) * mm});
            skLineSegment(sketch, "E345", {"start": v(-22.37, 3.06) * mm, "end": v(-22.02, 2.82) * mm});
            skLineSegment(sketch, "E346", {"start": v(-22.02, 2.82) * mm, "end": v(-21.63, 2.6) * mm});
            skLineSegment(sketch, "E347", {"start": v(-21.63, 2.6) * mm, "end": v(-21.25, 2.43) * mm});
            skLineSegment(sketch, "E348", {"start": v(-21.25, 2.43) * mm, "end": v(-20.84, 2.26) * mm});
            skLineSegment(sketch, "E349", {"start": v(-20.84, 2.26) * mm, "end": v(-20.44, 2.13) * mm});
            skLineSegment(sketch, "E350", {"start": v(-20.44, 2.13) * mm, "end": v(-20.02, 2.08) * mm});
            skLineSegment(sketch, "E351", {"start": v(-20.02, 2.08) * mm, "end": v(-19.6, 2.03) * mm});
            skLineSegment(sketch, "E352", {"start": v(-19.6, 2.03) * mm, "end": v(-19.17, 1.98) * mm});
            skLineSegment(sketch, "E353", {"start": v(-19.17, 1.98) * mm, "end": v(-18.75, 1.92) * mm});
            skLineSegment(sketch, "E354", {"start": v(-18.75, 1.92) * mm, "end": v(-18.32, 1.87) * mm});
            skLineSegment(sketch, "E355", {"start": v(-18.32, 1.87) * mm, "end": v(-17.9, 1.82) * mm});
            skLineSegment(sketch, "E356", {"start": v(-17.9, 1.82) * mm, "end": v(-17.47, 1.77) * mm});
            skLineSegment(sketch, "E357", {"start": v(-17.47, 1.77) * mm, "end": v(-17.05, 1.72) * mm});
            skLineSegment(sketch, "E358", {"start": v(-17.05, 1.72) * mm, "end": v(-16.63, 1.67) * mm});
            skLineSegment(sketch, "E359", {"start": v(-16.63, 1.67) * mm, "end": v(-16.2, 1.62) * mm});
            skLineSegment(sketch, "E360", {"start": v(-16.2, 1.62) * mm, "end": v(-16.2, 1.17) * mm});
            skLineSegment(sketch, "E361", {"start": v(-16.2, 1.17) * mm, "end": v(-16.2, 0.73) * mm});
            skLineSegment(sketch, "E362", {"start": v(-16.2, 0.73) * mm, "end": v(-16.2, 0.29) * mm});
            skLineSegment(sketch, "E363", {"start": v(-16.2, 0.29) * mm, "end": v(-16.2, -0.16) * mm});
            skLineSegment(sketch, "E364", {"start": v(-16.2, -0.16) * mm, "end": v(-16.2, -0.6) * mm});
            skLineSegment(sketch, "E365", {"start": v(-16.2, -0.6) * mm, "end": v(-16.2, -1.04) * mm});
            skLineSegment(sketch, "E366", {"start": v(-16.2, -1.04) * mm, "end": v(-16.2, -1.48) * mm});
            skLineSegment(sketch, "E367", {"start": v(-16.2, -1.48) * mm, "end": v(-16.2, -1.62) * mm});
            skLineSegment(sketch, "E368", {"start": v(-16.2, -1.62) * mm, "end": v(-16.63, -1.67) * mm});
            skLineSegment(sketch, "E369", {"start": v(-16.63, -1.67) * mm, "end": v(-17.05, -1.72) * mm});
            skLineSegment(sketch, "E370", {"start": v(-17.05, -1.72) * mm, "end": v(-17.47, -1.77) * mm});
            skLineSegment(sketch, "E371", {"start": v(-17.47, -1.77) * mm, "end": v(-17.9, -1.82) * mm});
            skLineSegment(sketch, "E372", {"start": v(-17.9, -1.82) * mm, "end": v(-18.32, -1.87) * mm});
            skLineSegment(sketch, "E373", {"start": v(-18.32, -1.87) * mm, "end": v(-18.75, -1.92) * mm});
            skLineSegment(sketch, "E374", {"start": v(-18.75, -1.92) * mm, "end": v(-19.17, -1.98) * mm});
            skLineSegment(sketch, "E375", {"start": v(-19.17, -1.98) * mm, "end": v(-19.6, -2.03) * mm});
            skLineSegment(sketch, "E376", {"start": v(-19.6, -2.03) * mm, "end": v(-20.02, -2.08) * mm});
            skLineSegment(sketch, "E377", {"start": v(-20.02, -2.08) * mm, "end": v(-20.44, -2.13) * mm});
            skLineSegment(sketch, "E378", {"start": v(-20.44, -2.13) * mm, "end": v(-20.86, -2.27) * mm});
            skLineSegment(sketch, "E379", {"start": v(-20.86, -2.27) * mm, "end": v(-21.25, -2.43) * mm});
            skLineSegment(sketch, "E380", {"start": v(-21.25, -2.43) * mm, "end": v(-21.65, -2.62) * mm});
            skLineSegment(sketch, "E381", {"start": v(-21.65, -2.62) * mm, "end": v(-22.02, -2.82) * mm});
            skLineSegment(sketch, "E382", {"start": v(-22.02, -2.82) * mm, "end": v(-22.4, -3.07) * mm});
            skLineSegment(sketch, "E383", {"start": v(-22.4, -3.07) * mm, "end": v(-22.73, -3.32) * mm});
            skLineSegment(sketch, "E384", {"start": v(-22.73, -3.32) * mm, "end": v(-23.06, -3.61) * mm});
            skLineSegment(sketch, "E385", {"start": v(-23.06, -3.61) * mm, "end": v(-23.36, -3.9) * mm});
            skLineSegment(sketch, "E386", {"start": v(-23.36, -3.9) * mm, "end": v(-23.66, -4.24) * mm});
            skLineSegment(sketch, "E387", {"start": v(-23.66, -4.24) * mm, "end": v(-23.92, -4.57) * mm});
            skLineSegment(sketch, "E388", {"start": v(-23.92, -4.57) * mm, "end": v(-24.17, -4.93) * mm});
            skLineSegment(sketch, "E389", {"start": v(-24.17, -4.93) * mm, "end": v(-24.38, -5.3) * mm});
            skLineSegment(sketch, "E390", {"start": v(-24.38, -5.3) * mm, "end": v(-24, -5.53) * mm});
            skLineSegment(sketch, "E391", {"start": v(-24, -5.53) * mm, "end": v(-23.63, -5.73) * mm});
            skLineSegment(sketch, "E392", {"start": v(-23.63, -5.73) * mm, "end": v(-23.23, -5.9) * mm});
            skLineSegment(sketch, "E393", {"start": v(-23.23, -5.9) * mm, "end": v(-22.83, -6.06) * mm});
            skLineSegment(sketch, "E394", {"start": v(-22.83, -6.06) * mm, "end": v(-22.4, -6.18) * mm});
            skLineSegment(sketch, "E395", {"start": v(-22.4, -6.18) * mm, "end": v(-22, -6.28) * mm});
            skLineSegment(sketch, "E396", {"start": v(-22, -6.28) * mm, "end": v(-21.56, -6.35) * mm});
            skLineSegment(sketch, "E397", {"start": v(-21.56, -6.35) * mm, "end": v(-21.14, -6.39) * mm});
            skLineSegment(sketch, "E398", {"start": v(-21.14, -6.39) * mm, "end": v(-20.7, -6.4) * mm});
            skLineSegment(sketch, "E399", {"start": v(-20.7, -6.4) * mm, "end": v(-20.28, -6.39) * mm});
            skLineSegment(sketch, "E400", {"start": v(-20.28, -6.39) * mm, "end": v(-19.84, -6.34) * mm});
            skLineSegment(sketch, "E401", {"start": v(-19.84, -6.34) * mm, "end": v(-19.42, -6.27) * mm});
            skLineSegment(sketch, "E402", {"start": v(-19.42, -6.27) * mm, "end": v(-19.02, -6.12) * mm});
            skLineSegment(sketch, "E403", {"start": v(-19.02, -6.12) * mm, "end": v(-18.62, -5.97) * mm});
            skLineSegment(sketch, "E404", {"start": v(-18.62, -5.97) * mm, "end": v(-18.22, -5.81) * mm});
            skLineSegment(sketch, "E405", {"start": v(-18.22, -5.81) * mm, "end": v(-17.83, -5.66) * mm});
            skLineSegment(sketch, "E406", {"start": v(-17.83, -5.66) * mm, "end": v(-17.43, -5.51) * mm});
            skLineSegment(sketch, "E407", {"start": v(-17.43, -5.51) * mm, "end": v(-17.03, -5.36) * mm});
            skLineSegment(sketch, "E408", {"start": v(-17.03, -5.36) * mm, "end": v(-16.63, -5.2) * mm});
            skLineSegment(sketch, "E409", {"start": v(-16.63, -5.2) * mm, "end": v(-16.23, -5.06) * mm});
            skLineSegment(sketch, "E410", {"start": v(-16.23, -5.06) * mm, "end": v(-15.83, -4.9) * mm});
            skLineSegment(sketch, "E411", {"start": v(-15.83, -4.9) * mm, "end": v(-15.43, -4.75) * mm});
            skLineSegment(sketch, "E412", {"start": v(-15.43, -4.75) * mm, "end": v(-15.22, -5.15) * mm});
            skLineSegment(sketch, "E413", {"start": v(-15.22, -5.15) * mm, "end": v(-15.02, -5.54) * mm});
            skLineSegment(sketch, "E414", {"start": v(-15.02, -5.54) * mm, "end": v(-14.81, -5.93) * mm});
            skLineSegment(sketch, "E415", {"start": v(-14.81, -5.93) * mm, "end": v(-14.6, -6.32) * mm});
            skLineSegment(sketch, "E416", {"start": v(-14.6, -6.32) * mm, "end": v(-14.4, -6.71) * mm});
            skLineSegment(sketch, "E417", {"start": v(-14.4, -6.71) * mm, "end": v(-14.2, -7.1) * mm});
            skLineSegment(sketch, "E418", {"start": v(-14.2, -7.1) * mm, "end": v(-13.99, -7.5) * mm});
            skLineSegment(sketch, "E419", {"start": v(-13.99, -7.5) * mm, "end": v(-13.93, -7.62) * mm});
            skLineSegment(sketch, "E420", {"start": v(-13.93, -7.62) * mm, "end": v(-14.28, -7.86) * mm});
            skLineSegment(sketch, "E421", {"start": v(-14.28, -7.86) * mm, "end": v(-14.63, -8.1) * mm});
            skLineSegment(sketch, "E422", {"start": v(-14.63, -8.1) * mm, "end": v(-14.98, -8.34) * mm});
            skLineSegment(sketch, "E423", {"start": v(-14.98, -8.34) * mm, "end": v(-15.33, -8.59) * mm});
            skLineSegment(sketch, "E424", {"start": v(-15.33, -8.59) * mm, "end": v(-15.68, -8.83) * mm});
            skLineSegment(sketch, "E425", {"start": v(-15.68, -8.83) * mm, "end": v(-16.04, -9.07) * mm});
            skLineSegment(sketch, "E426", {"start": v(-16.04, -9.07) * mm, "end": v(-16.39, -9.31) * mm});
            skLineSegment(sketch, "E427", {"start": v(-16.39, -9.31) * mm, "end": v(-16.74, -9.56) * mm});
            skLineSegment(sketch, "E428", {"start": v(-16.74, -9.56) * mm, "end": v(-17.1, -9.8) * mm});
            skLineSegment(sketch, "E429", {"start": v(-17.1, -9.8) * mm, "end": v(-17.44, -10.04) * mm});
            skLineSegment(sketch, "E430", {"start": v(-17.44, -10.04) * mm, "end": v(-17.75, -10.36) * mm});
            skLineSegment(sketch, "E431", {"start": v(-17.75, -10.36) * mm, "end": v(-18.02, -10.68) * mm});
            skLineSegment(sketch, "E432", {"start": v(-18.02, -10.68) * mm, "end": v(-18.29, -11.04) * mm});
            skLineSegment(sketch, "E433", {"start": v(-18.29, -11.04) * mm, "end": v(-18.52, -11.39) * mm});
            skLineSegment(sketch, "E434", {"start": v(-18.52, -11.39) * mm, "end": v(-18.73, -11.78) * mm});
            skLineSegment(sketch, "E435", {"start": v(-18.73, -11.78) * mm, "end": v(-18.91, -12.16) * mm});
            skLineSegment(sketch, "E436", {"start": v(-18.91, -12.16) * mm, "end": v(-19.07, -12.57) * mm});
            skLineSegment(sketch, "E437", {"start": v(-19.07, -12.57) * mm, "end": v(-19.2, -12.97) * mm});
            skLineSegment(sketch, "E438", {"start": v(-19.2, -12.97) * mm, "end": v(-19.31, -13.4) * mm});
            skLineSegment(sketch, "E439", {"start": v(-19.31, -13.4) * mm, "end": v(-19.39, -13.81) * mm});
            skLineSegment(sketch, "E440", {"start": v(-19.39, -13.81) * mm, "end": v(-19.44, -14.25) * mm});
            skLineSegment(sketch, "E441", {"start": v(-19.44, -14.25) * mm, "end": v(-19.46, -14.67) * mm});
            skLineSegment(sketch, "E442", {"start": v(-19.46, -14.67) * mm, "end": v(-19.02, -14.7) * mm});
            skLineSegment(sketch, "E443", {"start": v(-19.02, -14.7) * mm, "end": v(-18.6, -14.7) * mm});
            skLineSegment(sketch, "E444", {"start": v(-18.6, -14.7) * mm, "end": v(-18.15, -14.68) * mm});
            skLineSegment(sketch, "E445", {"start": v(-18.15, -14.68) * mm, "end": v(-17.74, -14.63) * mm});
            skLineSegment(sketch, "E446", {"start": v(-17.74, -14.63) * mm, "end": v(-17.3, -14.54) * mm});
            skLineSegment(sketch, "E447", {"start": v(-17.3, -14.54) * mm, "end": v(-16.9, -14.44) * mm});
            skLineSegment(sketch, "E448", {"start": v(-16.9, -14.44) * mm, "end": v(-16.47, -14.3) * mm});
            skLineSegment(sketch, "E449", {"start": v(-16.47, -14.3) * mm, "end": v(-16.08, -14.14) * mm});
            skLineSegment(sketch, "E450", {"start": v(-16.08, -14.14) * mm, "end": v(-15.69, -13.94) * mm});
            skLineSegment(sketch, "E451", {"start": v(-15.69, -13.94) * mm, "end": v(-15.32, -13.73) * mm});
            skLineSegment(sketch, "E452", {"start": v(-15.32, -13.73) * mm, "end": v(-14.95, -13.49) * mm});
            skLineSegment(sketch, "E453", {"start": v(-14.95, -13.49) * mm, "end": v(-14.62, -13.23) * mm});
            skLineSegment(sketch, "E454", {"start": v(-14.62, -13.23) * mm, "end": v(-14.33, -12.91) * mm});
            skLineSegment(sketch, "E455", {"start": v(-14.33, -12.91) * mm, "end": v(-14.05, -12.6) * mm});
            skLineSegment(sketch, "E456", {"start": v(-14.05, -12.6) * mm, "end": v(-13.77, -12.27) * mm});
            skLineSegment(sketch, "E457", {"start": v(-13.77, -12.27) * mm, "end": v(-13.48, -11.95) * mm});
            skLineSegment(sketch, "E458", {"start": v(-13.48, -11.95) * mm, "end": v(-13.2, -11.63) * mm});
            skLineSegment(sketch, "E459", {"start": v(-13.2, -11.63) * mm, "end": v(-12.92, -11.31) * mm});
            skLineSegment(sketch, "E460", {"start": v(-12.92, -11.31) * mm, "end": v(-12.63, -11) * mm});
            skLineSegment(sketch, "E461", {"start": v(-12.63, -11) * mm, "end": v(-12.35, -10.67) * mm});
            skLineSegment(sketch, "E462", {"start": v(-12.35, -10.67) * mm, "end": v(-12.07, -10.35) * mm});
            skLineSegment(sketch, "E463", {"start": v(-12.07, -10.35) * mm, "end": v(-11.78, -10.03) * mm});
            skLineSegment(sketch, "E464", {"start": v(-11.78, -10.03) * mm, "end": v(-11.42, -10.29) * mm});
            skLineSegment(sketch, "E465", {"start": v(-11.42, -10.29) * mm, "end": v(-11.05, -10.54) * mm});
            skLineSegment(sketch, "E466", {"start": v(-11.05, -10.54) * mm, "end": v(-10.7, -10.79) * mm});
            skLineSegment(sketch, "E467", {"start": v(-10.7, -10.79) * mm, "end": v(-10.33, -11.04) * mm});
            skLineSegment(sketch, "E468", {"start": v(-10.33, -11.04) * mm, "end": v(-9.96, -11.3) * mm});
            skLineSegment(sketch, "E469", {"start": v(-9.96, -11.3) * mm, "end": v(-9.6, -11.54) * mm});
            skLineSegment(sketch, "E470", {"start": v(-9.6, -11.54) * mm, "end": v(-9.23, -11.8) * mm});
            skLineSegment(sketch, "E471", {"start": v(-9.23, -11.8) * mm, "end": v(-9.12, -11.87) * mm});
            skLineSegment(sketch, "E472", {"start": v(-9.12, -11.87) * mm, "end": v(-9.32, -12.25) * mm});
            skLineSegment(sketch, "E473", {"start": v(-9.32, -12.25) * mm, "end": v(-9.52, -12.63) * mm});
            skLineSegment(sketch, "E474", {"start": v(-9.52, -12.63) * mm, "end": v(-9.72, -13) * mm});
            skLineSegment(sketch, "E475", {"start": v(-9.72, -13) * mm, "end": v(-9.92, -13.38) * mm});
            skLineSegment(sketch, "E476", {"start": v(-9.92, -13.38) * mm, "end": v(-10.12, -13.76) * mm});
            skLineSegment(sketch, "E477", {"start": v(-10.12, -13.76) * mm, "end": v(-10.32, -14.14) * mm});
            skLineSegment(sketch, "E478", {"start": v(-10.32, -14.14) * mm, "end": v(-10.51, -14.52) * mm});
            skLineSegment(sketch, "E479", {"start": v(-10.51, -14.52) * mm, "end": v(-10.71, -14.9) * mm});
            skLineSegment(sketch, "E480", {"start": v(-10.71, -14.9) * mm, "end": v(-10.91, -15.27) * mm});
            skLineSegment(sketch, "E481", {"start": v(-10.91, -15.27) * mm, "end": v(-11.1, -15.65) * mm});
            skLineSegment(sketch, "E482", {"start": v(-11.1, -15.65) * mm, "end": v(-11.23, -16.08) * mm});
            skLineSegment(sketch, "E483", {"start": v(-11.23, -16.08) * mm, "end": v(-11.33, -16.49) * mm});
            skLineSegment(sketch, "E484", {"start": v(-11.33, -16.49) * mm, "end": v(-11.4, -16.93) * mm});
            skLineSegment(sketch, "E485", {"start": v(-11.4, -16.93) * mm, "end": v(-11.44, -17.35) * mm});
            skLineSegment(sketch, "E486", {"start": v(-11.44, -17.35) * mm, "end": v(-11.44, -17.79) * mm});
            skLineSegment(sketch, "E487", {"start": v(-11.44, -17.79) * mm, "end": v(-11.43, -18.2) * mm});
            skLineSegment(sketch, "E488", {"start": v(-11.43, -18.2) * mm, "end": v(-11.38, -18.65) * mm});
            skLineSegment(sketch, "E489", {"start": v(-11.38, -18.65) * mm, "end": v(-11.31, -19.06) * mm});
            skLineSegment(sketch, "E490", {"start": v(-11.31, -19.06) * mm, "end": v(-11.2, -19.5) * mm});
            skLineSegment(sketch, "E491", {"start": v(-11.2, -19.5) * mm, "end": v(-11.08, -19.9) * mm});
            skLineSegment(sketch, "E492", {"start": v(-11.08, -19.9) * mm, "end": v(-10.92, -20.3) * mm});
            skLineSegment(sketch, "E493", {"start": v(-10.92, -20.3) * mm, "end": v(-10.74, -20.7) * mm});
            skLineSegment(sketch, "E494", {"start": v(-10.74, -20.7) * mm, "end": v(-10.34, -20.51) * mm});
            skLineSegment(sketch, "E495", {"start": v(-10.34, -20.51) * mm, "end": v(-9.96, -20.32) * mm});
            skLineSegment(sketch, "E496", {"start": v(-9.96, -20.32) * mm, "end": v(-9.58, -20.09) * mm});
            skLineSegment(sketch, "E497", {"start": v(-9.58, -20.09) * mm, "end": v(-9.24, -19.85) * mm});
            skLineSegment(sketch, "E498", {"start": v(-9.24, -19.85) * mm, "end": v(-8.9, -19.57) * mm});
            skLineSegment(sketch, "E499", {"start": v(-8.9, -19.57) * mm, "end": v(-8.58, -19.29) * mm});
            skLineSegment(sketch, "E500", {"start": v(-8.58, -19.29) * mm, "end": v(-8.28, -18.97) * mm});
            skLineSegment(sketch, "E501", {"start": v(-8.28, -18.97) * mm, "end": v(-8, -18.65) * mm});
            skLineSegment(sketch, "E502", {"start": v(-8, -18.65) * mm, "end": v(-7.74, -18.29) * mm});
            skLineSegment(sketch, "E503", {"start": v(-7.74, -18.29) * mm, "end": v(-7.51, -17.93) * mm});
            skLineSegment(sketch, "E504", {"start": v(-7.51, -17.93) * mm, "end": v(-7.3, -17.54) * mm});
            skLineSegment(sketch, "E505", {"start": v(-7.3, -17.54) * mm, "end": v(-7.12, -17.16) * mm});
            skLineSegment(sketch, "E506", {"start": v(-7.12, -17.16) * mm, "end": v(-7.02, -16.75) * mm});
            skLineSegment(sketch, "E507", {"start": v(-7.02, -16.75) * mm, "end": v(-6.92, -16.33) * mm});
            skLineSegment(sketch, "E508", {"start": v(-6.92, -16.33) * mm, "end": v(-6.82, -15.92) * mm});
            skLineSegment(sketch, "E509", {"start": v(-6.82, -15.92) * mm, "end": v(-6.72, -15.5) * mm});
            skLineSegment(sketch, "E510", {"start": v(-6.72, -15.5) * mm, "end": v(-6.61, -15.1) * mm});
            skLineSegment(sketch, "E511", {"start": v(-6.61, -15.1) * mm, "end": v(-6.51, -14.68) * mm});
            skLineSegment(sketch, "E512", {"start": v(-6.51, -14.68) * mm, "end": v(-6.4, -14.26) * mm});
            skLineSegment(sketch, "E513", {"start": v(-6.4, -14.26) * mm, "end": v(-6.3, -13.85) * mm});
            skLineSegment(sketch, "E514", {"start": v(-6.3, -13.85) * mm, "end": v(-6.2, -13.43) * mm});
            skLineSegment(sketch, "E515", {"start": v(-6.2, -13.43) * mm, "end": v(-6.1, -13.02) * mm});
            skLineSegment(sketch, "E516", {"start": v(-6.1, -13.02) * mm, "end": v(-5.66, -13.07) * mm});
            skLineSegment(sketch, "E517", {"start": v(-5.66, -13.07) * mm, "end": v(-5.22, -13.12) * mm});
            skLineSegment(sketch, "E518", {"start": v(-5.22, -13.12) * mm, "end": v(-4.78, -13.18) * mm});
            skLineSegment(sketch, "E519", {"start": v(-4.78, -13.18) * mm, "end": v(-4.34, -13.23) * mm});
            skLineSegment(sketch, "E520", {"start": v(-4.34, -13.23) * mm, "end": v(-3.9, -13.28) * mm});
            skLineSegment(sketch, "E521", {"start": v(-3.9, -13.28) * mm, "end": v(-3.46, -13.34) * mm});
            skLineSegment(sketch, "E522", {"start": v(-3.46, -13.34) * mm, "end": v(-3.02, -13.39) * mm});
            skLineSegment(sketch, "E523", {"start": v(-3.02, -13.39) * mm, "end": v(-2.9, -13.4) * mm});
            skLineSegment(sketch, "E524", {"start": v(-2.9, -13.4) * mm, "end": v(-2.9, -13.83) * mm});
            skLineSegment(sketch, "E525", {"start": v(-2.9, -13.83) * mm, "end": v(-2.9, -14.26) * mm});
            skLineSegment(sketch, "E526", {"start": v(-2.9, -14.26) * mm, "end": v(-2.9, -14.69) * mm});
            skLineSegment(sketch, "E527", {"start": v(-2.9, -14.69) * mm, "end": v(-2.9, -15.11) * mm});
            skLineSegment(sketch, "E528", {"start": v(-2.9, -15.11) * mm, "end": v(-2.9, -15.54) * mm});
            skLineSegment(sketch, "E529", {"start": v(-2.9, -15.54) * mm, "end": v(-2.9, -15.97) * mm});
            skLineSegment(sketch, "E530", {"start": v(-2.9, -15.97) * mm, "end": v(-2.9, -16.4) * mm});
            skLineSegment(sketch, "E531", {"start": v(-2.9, -16.4) * mm, "end": v(-2.9, -16.82) * mm});
            skLineSegment(sketch, "E532", {"start": v(-2.9, -16.82) * mm, "end": v(-2.9, -17.25) * mm});
            skLineSegment(sketch, "E533", {"start": v(-2.9, -17.25) * mm, "end": v(-2.9, -17.68) * mm});
            skLineSegment(sketch, "E534", {"start": v(-2.9, -17.68) * mm, "end": v(-2.8, -18.11) * mm});
            skLineSegment(sketch, "E535", {"start": v(-2.8, -18.11) * mm, "end": v(-2.7, -18.52) * mm});
            skLineSegment(sketch, "E536", {"start": v(-2.7, -18.52) * mm, "end": v(-2.56, -18.94) * mm});
            skLineSegment(sketch, "E537", {"start": v(-2.56, -18.94) * mm, "end": v(-2.4, -19.33) * mm});
            skLineSegment(sketch, "E538", {"start": v(-2.4, -19.33) * mm, "end": v(-2.2, -19.72) * mm});
            skLineSegment(sketch, "E539", {"start": v(-2.2, -19.72) * mm, "end": v(-1.99, -20.1) * mm});
            skLineSegment(sketch, "E540", {"start": v(-1.99, -20.1) * mm, "end": v(-1.74, -20.46) * mm});
            skLineSegment(sketch, "E541", {"start": v(-1.74, -20.46) * mm, "end": v(-1.49, -20.8) * mm});
            skLineSegment(sketch, "E542", {"start": v(-1.49, -20.8) * mm, "end": v(-1.2, -21.12) * mm});
            skLineSegment(sketch, "E543", {"start": v(-1.2, -21.12) * mm, "end": v(-0.9, -21.42) * mm});
            skLineSegment(sketch, "E544", {"start": v(-0.9, -21.42) * mm, "end": v(-0.56, -21.71) * mm});
            skLineSegment(sketch, "E545", {"start": v(-0.56, -21.71) * mm, "end": v(-0.23, -21.97) * mm});
            skLineSegment(sketch, "E546", {"start": v(-0.23, -21.97) * mm, "end": v(0.05, -21.62) * mm});
            skLineSegment(sketch, "E547", {"start": v(0.05, -21.62) * mm, "end": v(0.3, -21.28) * mm});
            skLineSegment(sketch, "E548", {"start": v(0.3, -21.28) * mm, "end": v(0.52, -20.9) * mm});
            skLineSegment(sketch, "E549", {"start": v(0.52, -20.9) * mm, "end": v(0.72, -20.52) * mm});
            skLineSegment(sketch, "E550", {"start": v(0.72, -20.52) * mm, "end": v(0.9, -20.12) * mm});
            skLineSegment(sketch, "E551", {"start": v(0.9, -20.12) * mm, "end": v(1.04, -19.72) * mm});
            skLineSegment(sketch, "E552", {"start": v(1.04, -19.72) * mm, "end": v(1.16, -19.3) * mm});
            skLineSegment(sketch, "E553", {"start": v(1.16, -19.3) * mm, "end": v(1.25, -18.89) * mm});
            skLineSegment(sketch, "E554", {"start": v(1.25, -18.89) * mm, "end": v(1.31, -18.45) * mm});
            skLineSegment(sketch, "E555", {"start": v(1.31, -18.45) * mm, "end": v(1.35, -18.03) * mm});
            skLineSegment(sketch, "E556", {"start": v(1.35, -18.03) * mm, "end": v(1.35, -17.58) * mm});
            skLineSegment(sketch, "E557", {"start": v(1.35, -17.58) * mm, "end": v(1.34, -17.16) * mm});
            skLineSegment(sketch, "E558", {"start": v(1.34, -17.16) * mm, "end": v(1.23, -16.75) * mm});
            skLineSegment(sketch, "E559", {"start": v(1.23, -16.75) * mm, "end": v(1.13, -16.33) * mm});
            skLineSegment(sketch, "E560", {"start": v(1.13, -16.33) * mm, "end": v(1.03, -15.92) * mm});
            skLineSegment(sketch, "E561", {"start": v(1.03, -15.92) * mm, "end": v(0.93, -15.5) * mm});
            skLineSegment(sketch, "E562", {"start": v(0.93, -15.5) * mm, "end": v(0.83, -15.1) * mm});
            skLineSegment(sketch, "E563", {"start": v(0.83, -15.1) * mm, "end": v(0.72, -14.68) * mm});
            skLineSegment(sketch, "E564", {"start": v(0.72, -14.68) * mm, "end": v(0.62, -14.26) * mm});
            skLineSegment(sketch, "E565", {"start": v(0.62, -14.26) * mm, "end": v(0.52, -13.85) * mm});
            skLineSegment(sketch, "E566", {"start": v(0.52, -13.85) * mm, "end": v(0.42, -13.43) * mm});
            skLineSegment(sketch, "E567", {"start": v(0.42, -13.43) * mm, "end": v(0.31, -13.02) * mm});
            skLineSegment(sketch, "E568", {"start": v(0.31, -13.02) * mm, "end": v(0.73, -12.86) * mm});
            skLineSegment(sketch, "E569", {"start": v(0.73, -12.86) * mm, "end": v(1.14, -12.7) * mm});
            skLineSegment(sketch, "E570", {"start": v(1.14, -12.7) * mm, "end": v(1.56, -12.54) * mm});
            skLineSegment(sketch, "E571", {"start": v(1.56, -12.54) * mm, "end": v(1.97, -12.39) * mm});
            skLineSegment(sketch, "E572", {"start": v(1.97, -12.39) * mm, "end": v(2.38, -12.23) * mm});
            skLineSegment(sketch, "E573", {"start": v(2.38, -12.23) * mm, "end": v(2.8, -12.07) * mm});
            skLineSegment(sketch, "E574", {"start": v(2.8, -12.07) * mm, "end": v(3.21, -11.92) * mm});
            skLineSegment(sketch, "E575", {"start": v(3.21, -11.92) * mm, "end": v(3.34, -11.87) * mm});
            skLineSegment(sketch, "E576", {"start": v(3.34, -11.87) * mm, "end": v(3.53, -12.25) * mm});
            skLineSegment(sketch, "E577", {"start": v(3.53, -12.25) * mm, "end": v(3.73, -12.63) * mm});
            skLineSegment(sketch, "E578", {"start": v(3.73, -12.63) * mm, "end": v(3.93, -13) * mm});
            skLineSegment(sketch, "E579", {"start": v(3.93, -13) * mm, "end": v(4.13, -13.38) * mm});
            skLineSegment(sketch, "E580", {"start": v(4.13, -13.38) * mm, "end": v(4.33, -13.76) * mm});
            skLineSegment(sketch, "E581", {"start": v(4.33, -13.76) * mm, "end": v(4.53, -14.14) * mm});
            skLineSegment(sketch, "E582", {"start": v(4.53, -14.14) * mm, "end": v(4.73, -14.52) * mm});
            skLineSegment(sketch, "E583", {"start": v(4.73, -14.52) * mm, "end": v(4.92, -14.9) * mm});
            skLineSegment(sketch, "E584", {"start": v(4.92, -14.9) * mm, "end": v(5.12, -15.27) * mm});
            skLineSegment(sketch, "E585", {"start": v(5.12, -15.27) * mm, "end": v(5.32, -15.65) * mm});
            skLineSegment(sketch, "E586", {"start": v(5.32, -15.65) * mm, "end": v(5.6, -16) * mm});
            skLineSegment(sketch, "E587", {"start": v(5.6, -16) * mm, "end": v(5.88, -16.3) * mm});
            skLineSegment(sketch, "E588", {"start": v(5.88, -16.3) * mm, "end": v(6.2, -16.61) * mm});
            skLineSegment(sketch, "E589", {"start": v(6.2, -16.61) * mm, "end": v(6.53, -16.88) * mm});
            skLineSegment(sketch, "E590", {"start": v(6.53, -16.88) * mm, "end": v(6.89, -17.14) * mm});
            skLineSegment(sketch, "E591", {"start": v(6.89, -17.14) * mm, "end": v(7.24, -17.37) * mm});
            skLineSegment(sketch, "E592", {"start": v(7.24, -17.37) * mm, "end": v(7.63, -17.58) * mm});
            skLineSegment(sketch, "E593", {"start": v(7.63, -17.58) * mm, "end": v(8.01, -17.76) * mm});
            skLineSegment(sketch, "E594", {"start": v(8.01, -17.76) * mm, "end": v(8.43, -17.91) * mm});
            skLineSegment(sketch, "E595", {"start": v(8.43, -17.91) * mm, "end": v(8.83, -18.04) * mm});
            skLineSegment(sketch, "E596", {"start": v(8.83, -18.04) * mm, "end": v(9.26, -18.14) * mm});
            skLineSegment(sketch, "E597", {"start": v(9.26, -18.14) * mm, "end": v(9.68, -18.21) * mm});
            skLineSegment(sketch, "E598", {"start": v(9.68, -18.21) * mm, "end": v(9.76, -17.78) * mm});
            skLineSegment(sketch, "E599", {"start": v(9.76, -17.78) * mm, "end": v(9.82, -17.36) * mm});
            skLineSegment(sketch, "E600", {"start": v(9.82, -17.36) * mm, "end": v(9.84, -16.92) * mm});
            skLineSegment(sketch, "E601", {"start": v(9.84, -16.92) * mm, "end": v(9.84, -16.5) * mm});
            skLineSegment(sketch, "E602", {"start": v(9.84, -16.5) * mm, "end": v(9.8, -16.05) * mm});
            skLineSegment(sketch, "E603", {"start": v(9.8, -16.05) * mm, "end": v(9.75, -15.64) * mm});
            skLineSegment(sketch, "E604", {"start": v(9.75, -15.64) * mm, "end": v(9.66, -15.2) * mm});
            skLineSegment(sketch, "E605", {"start": v(9.66, -15.2) * mm, "end": v(9.55, -14.8) * mm});
            skLineSegment(sketch, "E606", {"start": v(9.55, -14.8) * mm, "end": v(9.4, -14.38) * mm});
            skLineSegment(sketch, "E607", {"start": v(9.4, -14.38) * mm, "end": v(9.24, -14) * mm});
            skLineSegment(sketch, "E608", {"start": v(9.24, -14) * mm, "end": v(9.04, -13.6) * mm});
            skLineSegment(sketch, "E609", {"start": v(9.04, -13.6) * mm, "end": v(8.83, -13.23) * mm});
            skLineSegment(sketch, "E610", {"start": v(8.83, -13.23) * mm, "end": v(8.55, -12.91) * mm});
            skLineSegment(sketch, "E611", {"start": v(8.55, -12.91) * mm, "end": v(8.26, -12.6) * mm});
            skLineSegment(sketch, "E612", {"start": v(8.26, -12.6) * mm, "end": v(7.98, -12.27) * mm});
            skLineSegment(sketch, "E613", {"start": v(7.98, -12.27) * mm, "end": v(7.7, -11.95) * mm});
            skLineSegment(sketch, "E614", {"start": v(7.7, -11.95) * mm, "end": v(7.41, -11.63) * mm});
            skLineSegment(sketch, "E615", {"start": v(7.41, -11.63) * mm, "end": v(7.13, -11.31) * mm});
            skLineSegment(sketch, "E616", {"start": v(7.13, -11.31) * mm, "end": v(6.85, -11) * mm});
            skLineSegment(sketch, "E617", {"start": v(6.85, -11) * mm, "end": v(6.56, -10.67) * mm});
            skLineSegment(sketch, "E618", {"start": v(6.56, -10.67) * mm, "end": v(6.28, -10.35) * mm});
            skLineSegment(sketch, "E619", {"start": v(6.28, -10.35) * mm, "end": v(6, -10.03) * mm});
            skLineSegment(sketch, "E620", {"start": v(6, -10.03) * mm, "end": v(6.29, -9.7) * mm});
            skLineSegment(sketch, "E621", {"start": v(6.29, -9.7) * mm, "end": v(6.58, -9.37) * mm});
            skLineSegment(sketch, "E622", {"start": v(6.58, -9.37) * mm, "end": v(6.88, -9.04) * mm});
            skLineSegment(sketch, "E623", {"start": v(6.88, -9.04) * mm, "end": v(7.17, -8.7) * mm});
            skLineSegment(sketch, "E624", {"start": v(7.17, -8.7) * mm, "end": v(7.46, -8.38) * mm});
            skLineSegment(sketch, "E625", {"start": v(7.46, -8.38) * mm, "end": v(7.76, -8.04) * mm});
            skLineSegment(sketch, "E626", {"start": v(7.76, -8.04) * mm, "end": v(8.05, -7.71) * mm});
            skLineSegment(sketch, "E627", {"start": v(8.05, -7.71) * mm, "end": v(8.14, -7.62) * mm});
            skLineSegment(sketch, "E628", {"start": v(8.14, -7.62) * mm, "end": v(8.5, -7.86) * mm});
            skLineSegment(sketch, "E629", {"start": v(8.5, -7.86) * mm, "end": v(8.84, -8.1) * mm});
            skLineSegment(sketch, "E630", {"start": v(8.84, -8.1) * mm, "end": v(9.2, -8.34) * mm});
            skLineSegment(sketch, "E631", {"start": v(9.2, -8.34) * mm, "end": v(9.54, -8.59) * mm});
            skLineSegment(sketch, "E632", {"start": v(9.54, -8.59) * mm, "end": v(9.9, -8.83) * mm});
            skLineSegment(sketch, "E633", {"start": v(9.9, -8.83) * mm, "end": v(10.25, -9.07) * mm});
            skLineSegment(sketch, "E634", {"start": v(10.25, -9.07) * mm, "end": v(10.6, -9.31) * mm});
            skLineSegment(sketch, "E635", {"start": v(10.6, -9.31) * mm, "end": v(10.95, -9.56) * mm});
            skLineSegment(sketch, "E636", {"start": v(10.95, -9.56) * mm, "end": v(11.3, -9.8) * mm});
            skLineSegment(sketch, "E637", {"start": v(11.3, -9.8) * mm, "end": v(11.65, -10.04) * mm});
            skLineSegment(sketch, "E638", {"start": v(11.65, -10.04) * mm, "end": v(12.06, -10.22) * mm});
            skLineSegment(sketch, "E639", {"start": v(12.06, -10.22) * mm, "end": v(12.46, -10.36) * mm});
            skLineSegment(sketch, "E640", {"start": v(12.46, -10.36) * mm, "end": v(12.88, -10.48) * mm});
            skLineSegment(sketch, "E641", {"start": v(12.88, -10.48) * mm, "end": v(13.3, -10.57) * mm});
            skLineSegment(sketch, "E642", {"start": v(13.3, -10.57) * mm, "end": v(13.73, -10.63) * mm});
            skLineSegment(sketch, "E643", {"start": v(13.73, -10.63) * mm, "end": v(14.15, -10.67) * mm});
            skLineSegment(sketch, "E644", {"start": v(14.15, -10.67) * mm, "end": v(14.6, -10.67) * mm});
            skLineSegment(sketch, "E645", {"start": v(14.6, -10.67) * mm, "end": v(15.02, -10.65) * mm});
            skLineSegment(sketch, "E646", {"start": v(15.02, -10.65) * mm, "end": v(15.46, -10.6) * mm});
            skLineSegment(sketch, "E647", {"start": v(15.46, -10.6) * mm, "end": v(15.87, -10.52) * mm});
            skLineSegment(sketch, "E648", {"start": v(15.87, -10.52) * mm, "end": v(16.3, -10.41) * mm});
            skLineSegment(sketch, "E649", {"start": v(16.3, -10.41) * mm, "end": v(16.7, -10.28) * mm});
            skLineSegment(sketch, "E650", {"start": v(16.7, -10.28) * mm, "end": v(16.57, -9.86) * mm});
            skLineSegment(sketch, "E651", {"start": v(16.57, -9.86) * mm, "end": v(16.43, -9.46) * mm});
            skLineSegment(sketch, "E652", {"start": v(16.43, -9.46) * mm, "end": v(16.24, -9.06) * mm});
            skLineSegment(sketch, "E653", {"start": v(16.24, -9.06) * mm, "end": v(16.05, -8.69) * mm});
            skLineSegment(sketch, "E654", {"start": v(16.05, -8.69) * mm, "end": v(15.81, -8.31) * mm});
            skLineSegment(sketch, "E655", {"start": v(15.81, -8.31) * mm, "end": v(15.57, -7.97) * mm});
            skLineSegment(sketch, "E656", {"start": v(15.57, -7.97) * mm, "end": v(15.29, -7.63) * mm});
            skLineSegment(sketch, "E657", {"start": v(15.29, -7.63) * mm, "end": v(15, -7.32) * mm});
            skLineSegment(sketch, "E658", {"start": v(15, -7.32) * mm, "end": v(14.68, -7.02) * mm});
            skLineSegment(sketch, "E659", {"start": v(14.68, -7.02) * mm, "end": v(14.35, -6.75) * mm});
            skLineSegment(sketch, "E660", {"start": v(14.35, -6.75) * mm, "end": v(14, -6.5) * mm});
            skLineSegment(sketch, "E661", {"start": v(14, -6.5) * mm, "end": v(13.63, -6.27) * mm});
            skLineSegment(sketch, "E662", {"start": v(13.63, -6.27) * mm, "end": v(13.24, -6.12) * mm});
            skLineSegment(sketch, "E663", {"start": v(13.24, -6.12) * mm, "end": v(12.84, -5.97) * mm});
            skLineSegment(sketch, "E664", {"start": v(12.84, -5.97) * mm, "end": v(12.44, -5.81) * mm});
            skLineSegment(sketch, "E665", {"start": v(12.44, -5.81) * mm, "end": v(12.04, -5.66) * mm});
            skLineSegment(sketch, "E666", {"start": v(12.04, -5.66) * mm, "end": v(11.64, -5.51) * mm});
            skLineSegment(sketch, "E667", {"start": v(11.64, -5.51) * mm, "end": v(11.24, -5.36) * mm});
            skLineSegment(sketch, "E668", {"start": v(11.24, -5.36) * mm, "end": v(10.84, -5.2) * mm});
            skLineSegment(sketch, "E669", {"start": v(10.84, -5.2) * mm, "end": v(10.44, -5.06) * mm});
            skLineSegment(sketch, "E670", {"start": v(10.44, -5.06) * mm, "end": v(10.04, -4.9) * mm});
            skLineSegment(sketch, "E671", {"start": v(10.04, -4.9) * mm, "end": v(9.64, -4.75) * mm});
            skLineSegment(sketch, "E672", {"start": v(9.64, -4.75) * mm, "end": v(9.75, -4.32) * mm});
            skLineSegment(sketch, "E673", {"start": v(9.75, -4.32) * mm, "end": v(9.85, -3.9) * mm});
            skLineSegment(sketch, "E674", {"start": v(9.85, -3.9) * mm, "end": v(9.96, -3.46) * mm});
            skLineSegment(sketch, "E675", {"start": v(9.96, -3.46) * mm, "end": v(10.06, -3.03) * mm});
            skLineSegment(sketch, "E676", {"start": v(10.06, -3.03) * mm, "end": v(10.17, -2.6) * mm});
            skLineSegment(sketch, "E677", {"start": v(10.17, -2.6) * mm, "end": v(10.28, -2.17) * mm});
            skLineSegment(sketch, "E678", {"start": v(10.28, -2.17) * mm, "end": v(10.38, -1.74) * mm});
            skLineSegment(sketch, "E679", {"start": v(10.38, -1.74) * mm, "end": v(10.41, -1.62) * mm});
            skLineSegment(sketch, "E680", {"start": v(-7.06, 1.65) * mm, "end": v(-6.95, 1.9) * mm});
            skLineSegment(sketch, "E681", {"start": v(-6.95, 1.9) * mm, "end": v(-6.82, 2.16) * mm});
            skLineSegment(sketch, "E682", {"start": v(-6.82, 2.16) * mm, "end": v(-6.68, 2.4) * mm});
            skLineSegment(sketch, "E683", {"start": v(-6.68, 2.4) * mm, "end": v(-6.52, 2.63) * mm});
            skLineSegment(sketch, "E684", {"start": v(-6.52, 2.63) * mm, "end": v(-6.35, 2.86) * mm});
            skLineSegment(sketch, "E685", {"start": v(-6.35, 2.86) * mm, "end": v(-6.16, 3.07) * mm});
            skLineSegment(sketch, "E686", {"start": v(-6.16, 3.07) * mm, "end": v(-5.96, 3.27) * mm});
            skLineSegment(sketch, "E687", {"start": v(-5.96, 3.27) * mm, "end": v(-5.75, 3.45) * mm});
            skLineSegment(sketch, "E688", {"start": v(-5.75, 3.45) * mm, "end": v(-5.53, 3.63) * mm});
            skLineSegment(sketch, "E689", {"start": v(-5.53, 3.63) * mm, "end": v(-5.3, 3.78) * mm});
            skLineSegment(sketch, "E690", {"start": v(-5.3, 3.78) * mm, "end": v(-5.05, 3.93) * mm});
            skLineSegment(sketch, "E691", {"start": v(-5.05, 3.93) * mm, "end": v(-4.8, 4.05) * mm});
            skLineSegment(sketch, "E692", {"start": v(-4.8, 4.05) * mm, "end": v(-4.54, 4.17) * mm});
            skLineSegment(sketch, "E693", {"start": v(-4.54, 4.17) * mm, "end": v(-4.3, 4.26) * mm});
            skLineSegment(sketch, "E694", {"start": v(-4.3, 4.26) * mm, "end": v(-4.37, 10.62) * mm});
            skLineSegment(sketch, "E695", {"start": v(-4.37, 10.62) * mm, "end": v(-4.9, 10.53) * mm});
            skLineSegment(sketch, "E696", {"start": v(-4.9, 10.53) * mm, "end": v(-5.56, 10.39) * mm});
            skLineSegment(sketch, "E697", {"start": v(-5.56, 10.39) * mm, "end": v(-6.2, 10.2) * mm});
            skLineSegment(sketch, "E698", {"start": v(-6.2, 10.2) * mm, "end": v(-6.84, 9.97) * mm});
            skLineSegment(sketch, "E699", {"start": v(-6.84, 9.97) * mm, "end": v(-7.46, 9.7) * mm});
            skLineSegment(sketch, "E700", {"start": v(-7.46, 9.7) * mm, "end": v(-8.06, 9.4) * mm});
            skLineSegment(sketch, "E701", {"start": v(-8.06, 9.4) * mm, "end": v(-8.64, 9.05) * mm});
            skLineSegment(sketch, "E702", {"start": v(-8.64, 9.05) * mm, "end": v(-9.2, 8.68) * mm});
            skLineSegment(sketch, "E703", {"start": v(-9.2, 8.68) * mm, "end": v(-9.73, 8.26) * mm});
            skLineSegment(sketch, "E704", {"start": v(-9.73, 8.26) * mm, "end": v(-10.23, 7.82) * mm});
            skLineSegment(sketch, "E705", {"start": v(-10.23, 7.82) * mm, "end": v(-10.71, 7.34) * mm});
            skLineSegment(sketch, "E706", {"start": v(-10.71, 7.34) * mm, "end": v(-11.16, 6.84) * mm});
            skLineSegment(sketch, "E707", {"start": v(-11.16, 6.84) * mm, "end": v(-11.57, 6.3) * mm});
            skLineSegment(sketch, "E708", {"start": v(-11.57, 6.3) * mm, "end": v(-11.95, 5.75) * mm});
            skLineSegment(sketch, "E709", {"start": v(-11.95, 5.75) * mm, "end": v(-12.3, 5.17) * mm});
            skLineSegment(sketch, "E710", {"start": v(-12.3, 5.17) * mm, "end": v(-12.6, 4.57) * mm});
            skLineSegment(sketch, "E711", {"start": v(-12.6, 4.57) * mm, "end": v(-12.86, 3.95) * mm});
            skLineSegment(sketch, "E712", {"start": v(-12.86, 3.95) * mm, "end": v(-13.1, 3.31) * mm});
            skLineSegment(sketch, "E713", {"start": v(-13.1, 3.31) * mm, "end": v(-13.28, 2.67) * mm});
            skLineSegment(sketch, "E714", {"start": v(-13.28, 2.67) * mm, "end": v(-13.43, 2) * mm});
            skLineSegment(sketch, "E715", {"start": v(-13.43, 2) * mm, "end": v(-13.51, 1.48) * mm});
            skLineSegment(sketch, "E716", {"start": v(-13.51, 1.48) * mm, "end": v(-7.15, 1.4) * mm});
            skLineSegment(sketch, "E717", {"start": v(-7.15, 1.4) * mm, "end": v(-7.06, 1.65) * mm});
            skLineSegment(sketch, "E718", {"start": v(7.72, 1.48) * mm, "end": v(7.64, 2) * mm});
            skLineSegment(sketch, "E719", {"start": v(7.64, 2) * mm, "end": v(7.5, 2.67) * mm});
            skLineSegment(sketch, "E720", {"start": v(7.5, 2.67) * mm, "end": v(7.3, 3.31) * mm});
            skLineSegment(sketch, "E721", {"start": v(7.3, 3.31) * mm, "end": v(7.08, 3.95) * mm});
            skLineSegment(sketch, "E722", {"start": v(7.08, 3.95) * mm, "end": v(6.8, 4.57) * mm});
            skLineSegment(sketch, "E723", {"start": v(6.8, 4.57) * mm, "end": v(6.5, 5.17) * mm});
            skLineSegment(sketch, "E724", {"start": v(6.5, 5.17) * mm, "end": v(6.16, 5.75) * mm});
            skLineSegment(sketch, "E725", {"start": v(6.16, 5.75) * mm, "end": v(5.78, 6.3) * mm});
            skLineSegment(sketch, "E726", {"start": v(5.78, 6.3) * mm, "end": v(5.37, 6.84) * mm});
            skLineSegment(sketch, "E727", {"start": v(5.37, 6.84) * mm, "end": v(4.92, 7.34) * mm});
            skLineSegment(sketch, "E728", {"start": v(4.92, 7.34) * mm, "end": v(4.45, 7.82) * mm});
            skLineSegment(sketch, "E729", {"start": v(4.45, 7.82) * mm, "end": v(3.94, 8.26) * mm});
            skLineSegment(sketch, "E730", {"start": v(3.94, 8.26) * mm, "end": v(3.4, 8.68) * mm});
            skLineSegment(sketch, "E731", {"start": v(3.4, 8.68) * mm, "end": v(2.85, 9.05) * mm});
            skLineSegment(sketch, "E732", {"start": v(2.85, 9.05) * mm, "end": v(2.27, 9.4) * mm});
            skLineSegment(sketch, "E733", {"start": v(2.27, 9.4) * mm, "end": v(1.67, 9.7) * mm});
            skLineSegment(sketch, "E734", {"start": v(1.67, 9.7) * mm, "end": v(1.05, 9.97) * mm});
            skLineSegment(sketch, "E735", {"start": v(1.05, 9.97) * mm, "end": v(0.42, 10.2) * mm});
            skLineSegment(sketch, "E736", {"start": v(0.42, 10.2) * mm, "end": v(-0.23, 10.39) * mm});
            skLineSegment(sketch, "E737", {"start": v(-0.23, 10.39) * mm, "end": v(-0.89, 10.53) * mm});
            skLineSegment(sketch, "E738", {"start": v(-0.89, 10.53) * mm, "end": v(-1.42, 10.62) * mm});
            skLineSegment(sketch, "E739", {"start": v(-1.42, 10.62) * mm, "end": v(-1.5, 4.26) * mm});
            skLineSegment(sketch, "E740", {"start": v(-1.5, 4.26) * mm, "end": v(-1.24, 4.17) * mm});
            skLineSegment(sketch, "E741", {"start": v(-1.24, 4.17) * mm, "end": v(-0.99, 4.05) * mm});
            skLineSegment(sketch, "E742", {"start": v(-0.99, 4.05) * mm, "end": v(-0.74, 3.93) * mm});
            skLineSegment(sketch, "E743", {"start": v(-0.74, 3.93) * mm, "end": v(-0.5, 3.78) * mm});
            skLineSegment(sketch, "E744", {"start": v(-0.5, 3.78) * mm, "end": v(-0.26, 3.63) * mm});
            skLineSegment(sketch, "E745", {"start": v(-0.26, 3.63) * mm, "end": v(-0.04, 3.45) * mm});
            skLineSegment(sketch, "E746", {"start": v(-0.04, 3.45) * mm, "end": v(0.17, 3.27) * mm});
            skLineSegment(sketch, "E747", {"start": v(0.17, 3.27) * mm, "end": v(0.37, 3.07) * mm});
            skLineSegment(sketch, "E748", {"start": v(0.37, 3.07) * mm, "end": v(0.56, 2.86) * mm});
            skLineSegment(sketch, "E749", {"start": v(0.56, 2.86) * mm, "end": v(0.73, 2.63) * mm});
            skLineSegment(sketch, "E750", {"start": v(0.73, 2.63) * mm, "end": v(0.89, 2.4) * mm});
            skLineSegment(sketch, "E751", {"start": v(0.89, 2.4) * mm, "end": v(1.03, 2.16) * mm});
            skLineSegment(sketch, "E752", {"start": v(1.03, 2.16) * mm, "end": v(1.16, 1.9) * mm});
            skLineSegment(sketch, "E753", {"start": v(1.16, 1.9) * mm, "end": v(1.27, 1.65) * mm});
            skLineSegment(sketch, "E754", {"start": v(1.27, 1.65) * mm, "end": v(1.36, 1.4) * mm});
            skLineSegment(sketch, "E755", {"start": v(1.36, 1.4) * mm, "end": v(7.72, 1.48) * mm});
            skLineSegment(sketch, "E756", {"start": v(-4.3, -4.26) * mm, "end": v(-4.54, -4.17) * mm});
            skLineSegment(sketch, "E757", {"start": v(-4.54, -4.17) * mm, "end": v(-4.8, -4.05) * mm});
            skLineSegment(sketch, "E758", {"start": v(-4.8, -4.05) * mm, "end": v(-5.05, -3.93) * mm});
            skLineSegment(sketch, "E759", {"start": v(-5.05, -3.93) * mm, "end": v(-5.3, -3.78) * mm});
            skLineSegment(sketch, "E760", {"start": v(-5.3, -3.78) * mm, "end": v(-5.53, -3.63) * mm});
            skLineSegment(sketch, "E761", {"start": v(-5.53, -3.63) * mm, "end": v(-5.75, -3.45) * mm});
            skLineSegment(sketch, "E762", {"start": v(-5.75, -3.45) * mm, "end": v(-5.96, -3.27) * mm});
            skLineSegment(sketch, "E763", {"start": v(-5.96, -3.27) * mm, "end": v(-6.16, -3.07) * mm});
            skLineSegment(sketch, "E764", {"start": v(-6.16, -3.07) * mm, "end": v(-6.35, -2.86) * mm});
            skLineSegment(sketch, "E765", {"start": v(-6.35, -2.86) * mm, "end": v(-6.52, -2.63) * mm});
            skLineSegment(sketch, "E766", {"start": v(-6.52, -2.63) * mm, "end": v(-6.68, -2.4) * mm});
            skLineSegment(sketch, "E767", {"start": v(-6.68, -2.4) * mm, "end": v(-6.82, -2.16) * mm});
            skLineSegment(sketch, "E768", {"start": v(-6.82, -2.16) * mm, "end": v(-6.95, -1.9) * mm});
            skLineSegment(sketch, "E769", {"start": v(-6.95, -1.9) * mm, "end": v(-7.06, -1.65) * mm});
            skLineSegment(sketch, "E770", {"start": v(-7.06, -1.65) * mm, "end": v(-7.15, -1.4) * mm});
            skLineSegment(sketch, "E771", {"start": v(-7.15, -1.4) * mm, "end": v(-13.51, -1.48) * mm});
            skLineSegment(sketch, "E772", {"start": v(-13.51, -1.48) * mm, "end": v(-13.43, -2) * mm});
            skLineSegment(sketch, "E773", {"start": v(-13.43, -2) * mm, "end": v(-13.28, -2.67) * mm});
            skLineSegment(sketch, "E774", {"start": v(-13.28, -2.67) * mm, "end": v(-13.1, -3.31) * mm});
            skLineSegment(sketch, "E775", {"start": v(-13.1, -3.31) * mm, "end": v(-12.86, -3.95) * mm});
            skLineSegment(sketch, "E776", {"start": v(-12.86, -3.95) * mm, "end": v(-12.6, -4.57) * mm});
            skLineSegment(sketch, "E777", {"start": v(-12.6, -4.57) * mm, "end": v(-12.3, -5.17) * mm});
            skLineSegment(sketch, "E778", {"start": v(-12.3, -5.17) * mm, "end": v(-11.95, -5.75) * mm});
            skLineSegment(sketch, "E779", {"start": v(-11.95, -5.75) * mm, "end": v(-11.57, -6.3) * mm});
            skLineSegment(sketch, "E780", {"start": v(-11.57, -6.3) * mm, "end": v(-11.16, -6.84) * mm});
            skLineSegment(sketch, "E781", {"start": v(-11.16, -6.84) * mm, "end": v(-10.71, -7.34) * mm});
            skLineSegment(sketch, "E782", {"start": v(-10.71, -7.34) * mm, "end": v(-10.23, -7.82) * mm});
            skLineSegment(sketch, "E783", {"start": v(-10.23, -7.82) * mm, "end": v(-9.73, -8.26) * mm});
            skLineSegment(sketch, "E784", {"start": v(-9.73, -8.26) * mm, "end": v(-9.2, -8.68) * mm});
            skLineSegment(sketch, "E785", {"start": v(-9.2, -8.68) * mm, "end": v(-8.64, -9.05) * mm});
            skLineSegment(sketch, "E786", {"start": v(-8.64, -9.05) * mm, "end": v(-8.06, -9.4) * mm});
            skLineSegment(sketch, "E787", {"start": v(-8.06, -9.4) * mm, "end": v(-7.46, -9.7) * mm});
            skLineSegment(sketch, "E788", {"start": v(-7.46, -9.7) * mm, "end": v(-6.84, -9.97) * mm});
            skLineSegment(sketch, "E789", {"start": v(-6.84, -9.97) * mm, "end": v(-6.2, -10.2) * mm});
            skLineSegment(sketch, "E790", {"start": v(-6.2, -10.2) * mm, "end": v(-5.56, -10.39) * mm});
            skLineSegment(sketch, "E791", {"start": v(-5.56, -10.39) * mm, "end": v(-4.9, -10.53) * mm});
            skLineSegment(sketch, "E792", {"start": v(-4.9, -10.53) * mm, "end": v(-4.37, -10.62) * mm});
            skLineSegment(sketch, "E793", {"start": v(-4.37, -10.62) * mm, "end": v(-4.3, -4.26) * mm});
            skLineSegment(sketch, "E794", {"start": v(-0.89, -10.53) * mm, "end": v(-0.23, -10.39) * mm});
            skLineSegment(sketch, "E795", {"start": v(-0.23, -10.39) * mm, "end": v(0.42, -10.2) * mm});
            skLineSegment(sketch, "E796", {"start": v(0.42, -10.2) * mm, "end": v(1.05, -9.97) * mm});
            skLineSegment(sketch, "E797", {"start": v(1.05, -9.97) * mm, "end": v(1.67, -9.7) * mm});
            skLineSegment(sketch, "E798", {"start": v(1.67, -9.7) * mm, "end": v(2.27, -9.4) * mm});
            skLineSegment(sketch, "E799", {"start": v(2.27, -9.4) * mm, "end": v(2.85, -9.05) * mm});
            skLineSegment(sketch, "E800", {"start": v(2.85, -9.05) * mm, "end": v(3.4, -8.68) * mm});
            skLineSegment(sketch, "E801", {"start": v(3.4, -8.68) * mm, "end": v(3.94, -8.26) * mm});
            skLineSegment(sketch, "E802", {"start": v(3.94, -8.26) * mm, "end": v(4.45, -7.82) * mm});
            skLineSegment(sketch, "E803", {"start": v(4.45, -7.82) * mm, "end": v(4.92, -7.34) * mm});
            skLineSegment(sketch, "E804", {"start": v(4.92, -7.34) * mm, "end": v(5.37, -6.84) * mm});
            skLineSegment(sketch, "E805", {"start": v(5.37, -6.84) * mm, "end": v(5.78, -6.3) * mm});
            skLineSegment(sketch, "E806", {"start": v(5.78, -6.3) * mm, "end": v(6.16, -5.75) * mm});
            skLineSegment(sketch, "E807", {"start": v(6.16, -5.75) * mm, "end": v(6.5, -5.17) * mm});
            skLineSegment(sketch, "E808", {"start": v(6.5, -5.17) * mm, "end": v(6.8, -4.57) * mm});
            skLineSegment(sketch, "E809", {"start": v(6.8, -4.57) * mm, "end": v(7.08, -3.95) * mm});
            skLineSegment(sketch, "E810", {"start": v(7.08, -3.95) * mm, "end": v(7.3, -3.31) * mm});
            skLineSegment(sketch, "E811", {"start": v(7.3, -3.31) * mm, "end": v(7.5, -2.67) * mm});
            skLineSegment(sketch, "E812", {"start": v(7.5, -2.67) * mm, "end": v(7.64, -2) * mm});
            skLineSegment(sketch, "E813", {"start": v(7.64, -2) * mm, "end": v(7.72, -1.48) * mm});
            skLineSegment(sketch, "E814", {"start": v(7.72, -1.48) * mm, "end": v(1.36, -1.4) * mm});
            skLineSegment(sketch, "E815", {"start": v(1.36, -1.4) * mm, "end": v(1.27, -1.65) * mm});
            skLineSegment(sketch, "E816", {"start": v(1.27, -1.65) * mm, "end": v(1.16, -1.9) * mm});
            skLineSegment(sketch, "E817", {"start": v(1.16, -1.9) * mm, "end": v(1.03, -2.16) * mm});
            skLineSegment(sketch, "E818", {"start": v(1.03, -2.16) * mm, "end": v(0.89, -2.4) * mm});
            skLineSegment(sketch, "E819", {"start": v(0.89, -2.4) * mm, "end": v(0.73, -2.63) * mm});
            skLineSegment(sketch, "E820", {"start": v(0.73, -2.63) * mm, "end": v(0.56, -2.86) * mm});
            skLineSegment(sketch, "E821", {"start": v(0.56, -2.86) * mm, "end": v(0.37, -3.07) * mm});
            skLineSegment(sketch, "E822", {"start": v(0.37, -3.07) * mm, "end": v(0.17, -3.27) * mm});
            skLineSegment(sketch, "E823", {"start": v(0.17, -3.27) * mm, "end": v(-0.04, -3.45) * mm});
            skLineSegment(sketch, "E824", {"start": v(-0.04, -3.45) * mm, "end": v(-0.26, -3.63) * mm});
            skLineSegment(sketch, "E825", {"start": v(-0.26, -3.63) * mm, "end": v(-0.5, -3.78) * mm});
            skLineSegment(sketch, "E826", {"start": v(-0.5, -3.78) * mm, "end": v(-0.74, -3.93) * mm});
            skLineSegment(sketch, "E827", {"start": v(-0.74, -3.93) * mm, "end": v(-0.99, -4.05) * mm});
            skLineSegment(sketch, "E828", {"start": v(-0.99, -4.05) * mm, "end": v(-1.24, -4.17) * mm});
            skLineSegment(sketch, "E829", {"start": v(-1.24, -4.17) * mm, "end": v(-1.5, -4.26) * mm});
            skLineSegment(sketch, "E830", {"start": v(-1.5, -4.26) * mm, "end": v(-1.42, -10.62) * mm});
            skLineSegment(sketch, "E831", {"start": v(-1.42, -10.62) * mm, "end": v(-0.89, -10.53) * mm});
            skCircle(sketch, "E832", {"center": v(-2.9, 0) * mm, "radius": 2.65 * mm});
            skCircle(sketch, "E833", {"center": v(-2.9, 0) * mm, "radius": 6 * mm});
            skSolve(sketch);
        }
        {
            var Q0;
            Q0=makeQuery(id+"F0.imprint","IMPRINT",FACE,{"disambiguationData":[TD([[makeQuery(id+"F0.imprint","IMPRINT",EDGE,{"derivedFrom":sQuery(id+"F0.wireOp",EDGE,"E0")}),1.0]])]});
            var Q1;
            Q1=makeQuery(id+"F0.imprint","IMPRINT",FACE,{"disambiguationData":[TD([[makeQuery(id+"F0.imprint","IMPRINT",EDGE,{"derivedFrom":sQuery(id+"F0.wireOp",EDGE,"E680")}),-1.0]])]});
            var Q2;
            Q2=makeQuery(id+"F0.imprint","IMPRINT",FACE,{"disambiguationData":[TD([[makeQuery(id+"F0.imprint","IMPRINT",EDGE,{"derivedFrom":sQuery(id+"F0.wireOp",EDGE,"E680")}),1.0]])]});
            var Q3;
            {var subQ4=sQuery(id+"F0.wireOp",EDGE,"E740");Q3=makeQuery(id+"F0.imprint","IMPRINT",FACE,{"disambiguationData":[TD([[makeQuery(id+"F0.imprint","IMPRINT",EDGE,{"derivedFrom":subQ4}),1.0]])]});}
            var Q4;
            {var subQ0=sQuery(id+"F0.wireOp",EDGE,"E815");Q4=makeQuery(id+"F0.imprint","IMPRINT",FACE,{"disambiguationData":[TD([[makeQuery(id+"F0.imprint","IMPRINT",EDGE,{"derivedFrom":subQ0}),1.0]])]});}
            var Q5;
            {var subQ4=sQuery(id+"F0.wireOp",EDGE,"E756");Q5=makeQuery(id+"F0.imprint","IMPRINT",FACE,{"disambiguationData":[TD([[makeQuery(id+"F0.imprint","IMPRINT",EDGE,{"derivedFrom":subQ4}),1.0]])]});}
            extrude(context, id + "F1", {"entities" : qUnion([Q0, Q1, Q2, Q3, Q4, Q5]), "depth" : 8 * mm});
        }
        {
            var Q0;
            Q0=makeQuery(id+"F1.opExtrude","CAP_FACE",FACE,{"disambiguationData":[OSD([sQuery(id+"F0.wireOp",EDGE,"E0"),sQuery(id+"F0.wireOp",EDGE,"E1"),sQuery(id+"F0.wireOp",EDGE,"E2"),sQuery(id+"F0.wireOp",EDGE,"E3"),sQuery(id+"F0.wireOp",EDGE,"E4"),sQuery(id+"F0.wireOp",EDGE,"E5"),sQuery(id+"F0.wireOp",EDGE,"E6"),sQuery(id+"F0.wireOp",EDGE,"E7"),sQuery(id+"F0.wireOp",EDGE,"E8"),sQuery(id+"F0.wireOp",EDGE,"E9"),sQuery(id+"F0.wireOp",EDGE,"E10"),sQuery(id+"F0.wireOp",EDGE,"E11"),sQuery(id+"F0.wireOp",EDGE,"E12"),sQuery(id+"F0.wireOp",EDGE,"E13"),sQuery(id+"F0.wireOp",EDGE,"E14"),sQuery(id+"F0.wireOp",EDGE,"E15"),sQuery(id+"F0.wireOp",EDGE,"E16"),sQuery(id+"F0.wireOp",EDGE,"E17"),sQuery(id+"F0.wireOp",EDGE,"E18"),sQuery(id+"F0.wireOp",EDGE,"E19"),sQuery(id+"F0.wireOp",EDGE,"E20"),sQuery(id+"F0.wireOp",EDGE,"E21"),sQuery(id+"F0.wireOp",EDGE,"E22"),sQuery(id+"F0.wireOp",EDGE,"E23"),sQuery(id+"F0.wireOp",EDGE,"E24"),sQuery(id+"F0.wireOp",EDGE,"E25"),sQuery(id+"F0.wireOp",EDGE,"E26"),sQuery(id+"F0.wireOp",EDGE,"E27"),sQuery(id+"F0.wireOp",EDGE,"E28"),sQuery(id+"F0.wireOp",EDGE,"E29"),sQuery(id+"F0.wireOp",EDGE,"E30"),sQuery(id+"F0.wireOp",EDGE,"E31"),sQuery(id+"F0.wireOp",EDGE,"E32"),sQuery(id+"F0.wireOp",EDGE,"E33"),sQuery(id+"F0.wireOp",EDGE,"E34"),sQuery(id+"F0.wireOp",EDGE,"E35"),sQuery(id+"F0.wireOp",EDGE,"E36"),sQuery(id+"F0.wireOp",EDGE,"E37"),sQuery(id+"F0.wireOp",EDGE,"E38"),sQuery(id+"F0.wireOp",EDGE,"E39"),sQuery(id+"F0.wireOp",EDGE,"E40"),sQuery(id+"F0.wireOp",EDGE,"E41"),sQuery(id+"F0.wireOp",EDGE,"E42"),sQuery(id+"F0.wireOp",EDGE,"E43"),sQuery(id+"F0.wireOp",EDGE,"E44"),sQuery(id+"F0.wireOp",EDGE,"E45"),sQuery(id+"F0.wireOp",EDGE,"E46"),sQuery(id+"F0.wireOp",EDGE,"E47"),sQuery(id+"F0.wireOp",EDGE,"E48"),sQuery(id+"F0.wireOp",EDGE,"E49"),sQuery(id+"F0.wireOp",EDGE,"E50"),sQuery(id+"F0.wireOp",EDGE,"E51"),sQuery(id+"F0.wireOp",EDGE,"E52"),sQuery(id+"F0.wireOp",EDGE,"E53"),sQuery(id+"F0.wireOp",EDGE,"E54"),sQuery(id+"F0.wireOp",EDGE,"E55"),sQuery(id+"F0.wireOp",EDGE,"E56"),sQuery(id+"F0.wireOp",EDGE,"E57"),sQuery(id+"F0.wireOp",EDGE,"E58"),sQuery(id+"F0.wireOp",EDGE,"E59"),sQuery(id+"F0.wireOp",EDGE,"E60"),sQuery(id+"F0.wireOp",EDGE,"E61"),sQuery(id+"F0.wireOp",EDGE,"E62"),sQuery(id+"F0.wireOp",EDGE,"E63"),sQuery(id+"F0.wireOp",EDGE,"E64"),sQuery(id+"F0.wireOp",EDGE,"E65"),sQuery(id+"F0.wireOp",EDGE,"E66"),sQuery(id+"F0.wireOp",EDGE,"E67"),sQuery(id+"F0.wireOp",EDGE,"E68"),sQuery(id+"F0.wireOp",EDGE,"E69"),sQuery(id+"F0.wireOp",EDGE,"E70"),sQuery(id+"F0.wireOp",EDGE,"E71"),sQuery(id+"F0.wireOp",EDGE,"E72"),sQuery(id+"F0.wireOp",EDGE,"E73"),sQuery(id+"F0.wireOp",EDGE,"E74"),sQuery(id+"F0.wireOp",EDGE,"E75"),sQuery(id+"F0.wireOp",EDGE,"E76"),sQuery(id+"F0.wireOp",EDGE,"E77"),sQuery(id+"F0.wireOp",EDGE,"E78"),sQuery(id+"F0.wireOp",EDGE,"E79"),sQuery(id+"F0.wireOp",EDGE,"E80"),sQuery(id+"F0.wireOp",EDGE,"E81"),sQuery(id+"F0.wireOp",EDGE,"E82"),sQuery(id+"F0.wireOp",EDGE,"E83"),sQuery(id+"F0.wireOp",EDGE,"E84"),sQuery(id+"F0.wireOp",EDGE,"E85"),sQuery(id+"F0.wireOp",EDGE,"E86"),sQuery(id+"F0.wireOp",EDGE,"E87"),sQuery(id+"F0.wireOp",EDGE,"E88"),sQuery(id+"F0.wireOp",EDGE,"E89"),sQuery(id+"F0.wireOp",EDGE,"E90"),sQuery(id+"F0.wireOp",EDGE,"E91"),sQuery(id+"F0.wireOp",EDGE,"E92"),sQuery(id+"F0.wireOp",EDGE,"E93"),sQuery(id+"F0.wireOp",EDGE,"E94"),sQuery(id+"F0.wireOp",EDGE,"E95"),sQuery(id+"F0.wireOp",EDGE,"E96"),sQuery(id+"F0.wireOp",EDGE,"E97"),sQuery(id+"F0.wireOp",EDGE,"E98"),sQuery(id+"F0.wireOp",EDGE,"E99"),sQuery(id+"F0.wireOp",EDGE,"E100"),sQuery(id+"F0.wireOp",EDGE,"E101"),sQuery(id+"F0.wireOp",EDGE,"E102"),sQuery(id+"F0.wireOp",EDGE,"E103"),sQuery(id+"F0.wireOp",EDGE,"E104"),sQuery(id+"F0.wireOp",EDGE,"E105"),sQuery(id+"F0.wireOp",EDGE,"E106"),sQuery(id+"F0.wireOp",EDGE,"E107"),sQuery(id+"F0.wireOp",EDGE,"E108"),sQuery(id+"F0.wireOp",EDGE,"E109"),sQuery(id+"F0.wireOp",EDGE,"E110"),sQuery(id+"F0.wireOp",EDGE,"E111"),sQuery(id+"F0.wireOp",EDGE,"E112"),sQuery(id+"F0.wireOp",EDGE,"E113"),sQuery(id+"F0.wireOp",EDGE,"E114"),sQuery(id+"F0.wireOp",EDGE,"E115"),sQuery(id+"F0.wireOp",EDGE,"E116"),sQuery(id+"F0.wireOp",EDGE,"E117"),sQuery(id+"F0.wireOp",EDGE,"E118"),sQuery(id+"F0.wireOp",EDGE,"E119"),sQuery(id+"F0.wireOp",EDGE,"E120"),sQuery(id+"F0.wireOp",EDGE,"E121"),sQuery(id+"F0.wireOp",EDGE,"E122"),sQuery(id+"F0.wireOp",EDGE,"E123"),sQuery(id+"F0.wireOp",EDGE,"E124"),sQuery(id+"F0.wireOp",EDGE,"E125"),sQuery(id+"F0.wireOp",EDGE,"E126"),sQuery(id+"F0.wireOp",EDGE,"E127"),sQuery(id+"F0.wireOp",EDGE,"E128"),sQuery(id+"F0.wireOp",EDGE,"E129"),sQuery(id+"F0.wireOp",EDGE,"E130"),sQuery(id+"F0.wireOp",EDGE,"E131"),sQuery(id+"F0.wireOp",EDGE,"E132"),sQuery(id+"F0.wireOp",EDGE,"E133"),sQuery(id+"F0.wireOp",EDGE,"E134"),sQuery(id+"F0.wireOp",EDGE,"E135"),sQuery(id+"F0.wireOp",EDGE,"E136"),sQuery(id+"F0.wireOp",EDGE,"E137"),sQuery(id+"F0.wireOp",EDGE,"E138"),sQuery(id+"F0.wireOp",EDGE,"E139"),sQuery(id+"F0.wireOp",EDGE,"E140"),sQuery(id+"F0.wireOp",EDGE,"E141"),sQuery(id+"F0.wireOp",EDGE,"E142"),sQuery(id+"F0.wireOp",EDGE,"E143"),sQuery(id+"F0.wireOp",EDGE,"E144"),sQuery(id+"F0.wireOp",EDGE,"E145"),sQuery(id+"F0.wireOp",EDGE,"E146"),sQuery(id+"F0.wireOp",EDGE,"E147"),sQuery(id+"F0.wireOp",EDGE,"E148"),sQuery(id+"F0.wireOp",EDGE,"E149"),sQuery(id+"F0.wireOp",EDGE,"E150"),sQuery(id+"F0.wireOp",EDGE,"E151"),sQuery(id+"F0.wireOp",EDGE,"E152"),sQuery(id+"F0.wireOp",EDGE,"E153"),sQuery(id+"F0.wireOp",EDGE,"E154"),sQuery(id+"F0.wireOp",EDGE,"E155"),sQuery(id+"F0.wireOp",EDGE,"E156"),sQuery(id+"F0.wireOp",EDGE,"E157"),sQuery(id+"F0.wireOp",EDGE,"E158"),sQuery(id+"F0.wireOp",EDGE,"E159"),sQuery(id+"F0.wireOp",EDGE,"E160"),sQuery(id+"F0.wireOp",EDGE,"E161"),sQuery(id+"F0.wireOp",EDGE,"E162"),sQuery(id+"F0.wireOp",EDGE,"E163"),sQuery(id+"F0.wireOp",EDGE,"E164"),sQuery(id+"F0.wireOp",EDGE,"E165"),sQuery(id+"F0.wireOp",EDGE,"E166"),sQuery(id+"F0.wireOp",EDGE,"E167"),sQuery(id+"F0.wireOp",EDGE,"E168"),sQuery(id+"F0.wireOp",EDGE,"E169"),sQuery(id+"F0.wireOp",EDGE,"E170"),sQuery(id+"F0.wireOp",EDGE,"E171"),sQuery(id+"F0.wireOp",EDGE,"E172"),sQuery(id+"F0.wireOp",EDGE,"E173"),sQuery(id+"F0.wireOp",EDGE,"E174"),sQuery(id+"F0.wireOp",EDGE,"E175"),sQuery(id+"F0.wireOp",EDGE,"E176"),sQuery(id+"F0.wireOp",EDGE,"E177"),sQuery(id+"F0.wireOp",EDGE,"E178"),sQuery(id+"F0.wireOp",EDGE,"E179"),sQuery(id+"F0.wireOp",EDGE,"E180"),sQuery(id+"F0.wireOp",EDGE,"E181"),sQuery(id+"F0.wireOp",EDGE,"E182"),sQuery(id+"F0.wireOp",EDGE,"E183"),sQuery(id+"F0.wireOp",EDGE,"E184"),sQuery(id+"F0.wireOp",EDGE,"E185"),sQuery(id+"F0.wireOp",EDGE,"E186"),sQuery(id+"F0.wireOp",EDGE,"E187"),sQuery(id+"F0.wireOp",EDGE,"E188"),sQuery(id+"F0.wireOp",EDGE,"E189"),sQuery(id+"F0.wireOp",EDGE,"E190"),sQuery(id+"F0.wireOp",EDGE,"E191"),sQuery(id+"F0.wireOp",EDGE,"E192"),sQuery(id+"F0.wireOp",EDGE,"E193"),sQuery(id+"F0.wireOp",EDGE,"E194"),sQuery(id+"F0.wireOp",EDGE,"E195"),sQuery(id+"F0.wireOp",EDGE,"E196"),sQuery(id+"F0.wireOp",EDGE,"E197"),sQuery(id+"F0.wireOp",EDGE,"E198"),sQuery(id+"F0.wireOp",EDGE,"E199"),sQuery(id+"F0.wireOp",EDGE,"E200"),sQuery(id+"F0.wireOp",EDGE,"E201"),sQuery(id+"F0.wireOp",EDGE,"E202"),sQuery(id+"F0.wireOp",EDGE,"E203"),sQuery(id+"F0.wireOp",EDGE,"E204"),sQuery(id+"F0.wireOp",EDGE,"E205"),sQuery(id+"F0.wireOp",EDGE,"E206"),sQuery(id+"F0.wireOp",EDGE,"E207"),sQuery(id+"F0.wireOp",EDGE,"E208"),sQuery(id+"F0.wireOp",EDGE,"E209"),sQuery(id+"F0.wireOp",EDGE,"E210"),sQuery(id+"F0.wireOp",EDGE,"E211"),sQuery(id+"F0.wireOp",EDGE,"E212"),sQuery(id+"F0.wireOp",EDGE,"E213"),sQuery(id+"F0.wireOp",EDGE,"E214"),sQuery(id+"F0.wireOp",EDGE,"E215"),sQuery(id+"F0.wireOp",EDGE,"E216"),sQuery(id+"F0.wireOp",EDGE,"E217"),sQuery(id+"F0.wireOp",EDGE,"E218"),sQuery(id+"F0.wireOp",EDGE,"E219"),sQuery(id+"F0.wireOp",EDGE,"E220"),sQuery(id+"F0.wireOp",EDGE,"E221"),sQuery(id+"F0.wireOp",EDGE,"E222"),sQuery(id+"F0.wireOp",EDGE,"E223"),sQuery(id+"F0.wireOp",EDGE,"E224"),sQuery(id+"F0.wireOp",EDGE,"E225"),sQuery(id+"F0.wireOp",EDGE,"E226"),sQuery(id+"F0.wireOp",EDGE,"E227"),sQuery(id+"F0.wireOp",EDGE,"E228"),sQuery(id+"F0.wireOp",EDGE,"E229"),sQuery(id+"F0.wireOp",EDGE,"E230"),sQuery(id+"F0.wireOp",EDGE,"E231"),sQuery(id+"F0.wireOp",EDGE,"E232"),sQuery(id+"F0.wireOp",EDGE,"E233"),sQuery(id+"F0.wireOp",EDGE,"E234"),sQuery(id+"F0.wireOp",EDGE,"E235"),sQuery(id+"F0.wireOp",EDGE,"E236"),sQuery(id+"F0.wireOp",EDGE,"E237"),sQuery(id+"F0.wireOp",EDGE,"E238"),sQuery(id+"F0.wireOp",EDGE,"E239"),sQuery(id+"F0.wireOp",EDGE,"E240"),sQuery(id+"F0.wireOp",EDGE,"E241"),sQuery(id+"F0.wireOp",EDGE,"E242"),sQuery(id+"F0.wireOp",EDGE,"E243"),sQuery(id+"F0.wireOp",EDGE,"E244"),sQuery(id+"F0.wireOp",EDGE,"E245"),sQuery(id+"F0.wireOp",EDGE,"E246"),sQuery(id+"F0.wireOp",EDGE,"E247"),sQuery(id+"F0.wireOp",EDGE,"E248"),sQuery(id+"F0.wireOp",EDGE,"E249"),sQuery(id+"F0.wireOp",EDGE,"E250"),sQuery(id+"F0.wireOp",EDGE,"E251"),sQuery(id+"F0.wireOp",EDGE,"E252"),sQuery(id+"F0.wireOp",EDGE,"E253"),sQuery(id+"F0.wireOp",EDGE,"E254"),sQuery(id+"F0.wireOp",EDGE,"E255"),sQuery(id+"F0.wireOp",EDGE,"E256"),sQuery(id+"F0.wireOp",EDGE,"E257"),sQuery(id+"F0.wireOp",EDGE,"E258"),sQuery(id+"F0.wireOp",EDGE,"E259"),sQuery(id+"F0.wireOp",EDGE,"E260"),sQuery(id+"F0.wireOp",EDGE,"E261"),sQuery(id+"F0.wireOp",EDGE,"E262"),sQuery(id+"F0.wireOp",EDGE,"E263"),sQuery(id+"F0.wireOp",EDGE,"E264"),sQuery(id+"F0.wireOp",EDGE,"E265"),sQuery(id+"F0.wireOp",EDGE,"E266"),sQuery(id+"F0.wireOp",EDGE,"E267"),sQuery(id+"F0.wireOp",EDGE,"E268"),sQuery(id+"F0.wireOp",EDGE,"E269"),sQuery(id+"F0.wireOp",EDGE,"E270"),sQuery(id+"F0.wireOp",EDGE,"E271"),sQuery(id+"F0.wireOp",EDGE,"E272"),sQuery(id+"F0.wireOp",EDGE,"E273"),sQuery(id+"F0.wireOp",EDGE,"E274"),sQuery(id+"F0.wireOp",EDGE,"E275"),sQuery(id+"F0.wireOp",EDGE,"E276"),sQuery(id+"F0.wireOp",EDGE,"E277"),sQuery(id+"F0.wireOp",EDGE,"E278"),sQuery(id+"F0.wireOp",EDGE,"E279"),sQuery(id+"F0.wireOp",EDGE,"E280"),sQuery(id+"F0.wireOp",EDGE,"E281"),sQuery(id+"F0.wireOp",EDGE,"E282"),sQuery(id+"F0.wireOp",EDGE,"E283"),sQuery(id+"F0.wireOp",EDGE,"E284"),sQuery(id+"F0.wireOp",EDGE,"E285"),sQuery(id+"F0.wireOp",EDGE,"E286"),sQuery(id+"F0.wireOp",EDGE,"E287"),sQuery(id+"F0.wireOp",EDGE,"E288"),sQuery(id+"F0.wireOp",EDGE,"E289"),sQuery(id+"F0.wireOp",EDGE,"E290"),sQuery(id+"F0.wireOp",EDGE,"E291"),sQuery(id+"F0.wireOp",EDGE,"E292"),sQuery(id+"F0.wireOp",EDGE,"E293"),sQuery(id+"F0.wireOp",EDGE,"E294"),sQuery(id+"F0.wireOp",EDGE,"E295"),sQuery(id+"F0.wireOp",EDGE,"E296"),sQuery(id+"F0.wireOp",EDGE,"E297"),sQuery(id+"F0.wireOp",EDGE,"E298"),sQuery(id+"F0.wireOp",EDGE,"E299"),sQuery(id+"F0.wireOp",EDGE,"E300"),sQuery(id+"F0.wireOp",EDGE,"E301"),sQuery(id+"F0.wireOp",EDGE,"E302"),sQuery(id+"F0.wireOp",EDGE,"E303"),sQuery(id+"F0.wireOp",EDGE,"E304"),sQuery(id+"F0.wireOp",EDGE,"E305"),sQuery(id+"F0.wireOp",EDGE,"E306"),sQuery(id+"F0.wireOp",EDGE,"E307"),sQuery(id+"F0.wireOp",EDGE,"E308"),sQuery(id+"F0.wireOp",EDGE,"E309"),sQuery(id+"F0.wireOp",EDGE,"E310"),sQuery(id+"F0.wireOp",EDGE,"E311"),sQuery(id+"F0.wireOp",EDGE,"E312"),sQuery(id+"F0.wireOp",EDGE,"E313"),sQuery(id+"F0.wireOp",EDGE,"E314"),sQuery(id+"F0.wireOp",EDGE,"E315"),sQuery(id+"F0.wireOp",EDGE,"E316"),sQuery(id+"F0.wireOp",EDGE,"E317"),sQuery(id+"F0.wireOp",EDGE,"E318"),sQuery(id+"F0.wireOp",EDGE,"E319"),sQuery(id+"F0.wireOp",EDGE,"E320"),sQuery(id+"F0.wireOp",EDGE,"E321"),sQuery(id+"F0.wireOp",EDGE,"E322"),sQuery(id+"F0.wireOp",EDGE,"E323"),sQuery(id+"F0.wireOp",EDGE,"E324"),sQuery(id+"F0.wireOp",EDGE,"E325"),sQuery(id+"F0.wireOp",EDGE,"E326"),sQuery(id+"F0.wireOp",EDGE,"E327"),sQuery(id+"F0.wireOp",EDGE,"E328"),sQuery(id+"F0.wireOp",EDGE,"E329"),sQuery(id+"F0.wireOp",EDGE,"E330"),sQuery(id+"F0.wireOp",EDGE,"E331"),sQuery(id+"F0.wireOp",EDGE,"E332"),sQuery(id+"F0.wireOp",EDGE,"E333"),sQuery(id+"F0.wireOp",EDGE,"E334"),sQuery(id+"F0.wireOp",EDGE,"E335"),sQuery(id+"F0.wireOp",EDGE,"E336"),sQuery(id+"F0.wireOp",EDGE,"E337"),sQuery(id+"F0.wireOp",EDGE,"E338"),sQuery(id+"F0.wireOp",EDGE,"E339"),sQuery(id+"F0.wireOp",EDGE,"E340"),sQuery(id+"F0.wireOp",EDGE,"E341"),sQuery(id+"F0.wireOp",EDGE,"E342"),sQuery(id+"F0.wireOp",EDGE,"E343"),sQuery(id+"F0.wireOp",EDGE,"E344"),sQuery(id+"F0.wireOp",EDGE,"E345"),sQuery(id+"F0.wireOp",EDGE,"E346"),sQuery(id+"F0.wireOp",EDGE,"E347"),sQuery(id+"F0.wireOp",EDGE,"E348"),sQuery(id+"F0.wireOp",EDGE,"E349"),sQuery(id+"F0.wireOp",EDGE,"E350"),sQuery(id+"F0.wireOp",EDGE,"E351"),sQuery(id+"F0.wireOp",EDGE,"E352"),sQuery(id+"F0.wireOp",EDGE,"E353"),sQuery(id+"F0.wireOp",EDGE,"E354"),sQuery(id+"F0.wireOp",EDGE,"E355"),sQuery(id+"F0.wireOp",EDGE,"E356"),sQuery(id+"F0.wireOp",EDGE,"E357"),sQuery(id+"F0.wireOp",EDGE,"E358"),sQuery(id+"F0.wireOp",EDGE,"E359"),sQuery(id+"F0.wireOp",EDGE,"E360"),sQuery(id+"F0.wireOp",EDGE,"E361"),sQuery(id+"F0.wireOp",EDGE,"E362"),sQuery(id+"F0.wireOp",EDGE,"E363"),sQuery(id+"F0.wireOp",EDGE,"E364"),sQuery(id+"F0.wireOp",EDGE,"E365"),sQuery(id+"F0.wireOp",EDGE,"E366"),sQuery(id+"F0.wireOp",EDGE,"E367"),sQuery(id+"F0.wireOp",EDGE,"E368"),sQuery(id+"F0.wireOp",EDGE,"E369"),sQuery(id+"F0.wireOp",EDGE,"E370"),sQuery(id+"F0.wireOp",EDGE,"E371"),sQuery(id+"F0.wireOp",EDGE,"E372"),sQuery(id+"F0.wireOp",EDGE,"E373"),sQuery(id+"F0.wireOp",EDGE,"E374"),sQuery(id+"F0.wireOp",EDGE,"E375"),sQuery(id+"F0.wireOp",EDGE,"E376"),sQuery(id+"F0.wireOp",EDGE,"E377"),sQuery(id+"F0.wireOp",EDGE,"E378"),sQuery(id+"F0.wireOp",EDGE,"E379"),sQuery(id+"F0.wireOp",EDGE,"E380"),sQuery(id+"F0.wireOp",EDGE,"E381"),sQuery(id+"F0.wireOp",EDGE,"E382"),sQuery(id+"F0.wireOp",EDGE,"E383"),sQuery(id+"F0.wireOp",EDGE,"E384"),sQuery(id+"F0.wireOp",EDGE,"E385"),sQuery(id+"F0.wireOp",EDGE,"E386"),sQuery(id+"F0.wireOp",EDGE,"E387"),sQuery(id+"F0.wireOp",EDGE,"E388"),sQuery(id+"F0.wireOp",EDGE,"E389"),sQuery(id+"F0.wireOp",EDGE,"E390"),sQuery(id+"F0.wireOp",EDGE,"E391"),sQuery(id+"F0.wireOp",EDGE,"E392"),sQuery(id+"F0.wireOp",EDGE,"E393"),sQuery(id+"F0.wireOp",EDGE,"E394"),sQuery(id+"F0.wireOp",EDGE,"E395"),sQuery(id+"F0.wireOp",EDGE,"E396"),sQuery(id+"F0.wireOp",EDGE,"E397"),sQuery(id+"F0.wireOp",EDGE,"E398"),sQuery(id+"F0.wireOp",EDGE,"E399"),sQuery(id+"F0.wireOp",EDGE,"E400"),sQuery(id+"F0.wireOp",EDGE,"E401"),sQuery(id+"F0.wireOp",EDGE,"E402"),sQuery(id+"F0.wireOp",EDGE,"E403"),sQuery(id+"F0.wireOp",EDGE,"E404"),sQuery(id+"F0.wireOp",EDGE,"E405"),sQuery(id+"F0.wireOp",EDGE,"E406"),sQuery(id+"F0.wireOp",EDGE,"E407"),sQuery(id+"F0.wireOp",EDGE,"E408"),sQuery(id+"F0.wireOp",EDGE,"E409"),sQuery(id+"F0.wireOp",EDGE,"E410"),sQuery(id+"F0.wireOp",EDGE,"E411"),sQuery(id+"F0.wireOp",EDGE,"E412"),sQuery(id+"F0.wireOp",EDGE,"E413"),sQuery(id+"F0.wireOp",EDGE,"E414"),sQuery(id+"F0.wireOp",EDGE,"E415"),sQuery(id+"F0.wireOp",EDGE,"E416"),sQuery(id+"F0.wireOp",EDGE,"E417"),sQuery(id+"F0.wireOp",EDGE,"E418"),sQuery(id+"F0.wireOp",EDGE,"E419"),sQuery(id+"F0.wireOp",EDGE,"E420"),sQuery(id+"F0.wireOp",EDGE,"E421"),sQuery(id+"F0.wireOp",EDGE,"E422"),sQuery(id+"F0.wireOp",EDGE,"E423"),sQuery(id+"F0.wireOp",EDGE,"E424"),sQuery(id+"F0.wireOp",EDGE,"E425"),sQuery(id+"F0.wireOp",EDGE,"E426"),sQuery(id+"F0.wireOp",EDGE,"E427"),sQuery(id+"F0.wireOp",EDGE,"E428"),sQuery(id+"F0.wireOp",EDGE,"E429"),sQuery(id+"F0.wireOp",EDGE,"E430"),sQuery(id+"F0.wireOp",EDGE,"E431"),sQuery(id+"F0.wireOp",EDGE,"E432"),sQuery(id+"F0.wireOp",EDGE,"E433"),sQuery(id+"F0.wireOp",EDGE,"E434"),sQuery(id+"F0.wireOp",EDGE,"E435"),sQuery(id+"F0.wireOp",EDGE,"E436"),sQuery(id+"F0.wireOp",EDGE,"E437"),sQuery(id+"F0.wireOp",EDGE,"E438"),sQuery(id+"F0.wireOp",EDGE,"E439"),sQuery(id+"F0.wireOp",EDGE,"E440"),sQuery(id+"F0.wireOp",EDGE,"E441"),sQuery(id+"F0.wireOp",EDGE,"E442"),sQuery(id+"F0.wireOp",EDGE,"E443"),sQuery(id+"F0.wireOp",EDGE,"E444"),sQuery(id+"F0.wireOp",EDGE,"E445"),sQuery(id+"F0.wireOp",EDGE,"E446"),sQuery(id+"F0.wireOp",EDGE,"E447"),sQuery(id+"F0.wireOp",EDGE,"E448"),sQuery(id+"F0.wireOp",EDGE,"E449"),sQuery(id+"F0.wireOp",EDGE,"E450"),sQuery(id+"F0.wireOp",EDGE,"E451"),sQuery(id+"F0.wireOp",EDGE,"E452"),sQuery(id+"F0.wireOp",EDGE,"E453"),sQuery(id+"F0.wireOp",EDGE,"E454"),sQuery(id+"F0.wireOp",EDGE,"E455"),sQuery(id+"F0.wireOp",EDGE,"E456"),sQuery(id+"F0.wireOp",EDGE,"E457"),sQuery(id+"F0.wireOp",EDGE,"E458"),sQuery(id+"F0.wireOp",EDGE,"E459"),sQuery(id+"F0.wireOp",EDGE,"E460"),sQuery(id+"F0.wireOp",EDGE,"E461"),sQuery(id+"F0.wireOp",EDGE,"E462"),sQuery(id+"F0.wireOp",EDGE,"E463"),sQuery(id+"F0.wireOp",EDGE,"E464"),sQuery(id+"F0.wireOp",EDGE,"E465"),sQuery(id+"F0.wireOp",EDGE,"E466"),sQuery(id+"F0.wireOp",EDGE,"E467"),sQuery(id+"F0.wireOp",EDGE,"E468"),sQuery(id+"F0.wireOp",EDGE,"E469"),sQuery(id+"F0.wireOp",EDGE,"E470"),sQuery(id+"F0.wireOp",EDGE,"E471"),sQuery(id+"F0.wireOp",EDGE,"E472"),sQuery(id+"F0.wireOp",EDGE,"E473"),sQuery(id+"F0.wireOp",EDGE,"E474"),sQuery(id+"F0.wireOp",EDGE,"E475"),sQuery(id+"F0.wireOp",EDGE,"E476"),sQuery(id+"F0.wireOp",EDGE,"E477"),sQuery(id+"F0.wireOp",EDGE,"E478"),sQuery(id+"F0.wireOp",EDGE,"E479"),sQuery(id+"F0.wireOp",EDGE,"E480"),sQuery(id+"F0.wireOp",EDGE,"E481"),sQuery(id+"F0.wireOp",EDGE,"E482"),sQuery(id+"F0.wireOp",EDGE,"E483"),sQuery(id+"F0.wireOp",EDGE,"E484"),sQuery(id+"F0.wireOp",EDGE,"E485"),sQuery(id+"F0.wireOp",EDGE,"E486"),sQuery(id+"F0.wireOp",EDGE,"E487"),sQuery(id+"F0.wireOp",EDGE,"E488"),sQuery(id+"F0.wireOp",EDGE,"E489"),sQuery(id+"F0.wireOp",EDGE,"E490"),sQuery(id+"F0.wireOp",EDGE,"E491"),sQuery(id+"F0.wireOp",EDGE,"E492"),sQuery(id+"F0.wireOp",EDGE,"E493"),sQuery(id+"F0.wireOp",EDGE,"E494"),sQuery(id+"F0.wireOp",EDGE,"E495"),sQuery(id+"F0.wireOp",EDGE,"E496"),sQuery(id+"F0.wireOp",EDGE,"E497"),sQuery(id+"F0.wireOp",EDGE,"E498"),sQuery(id+"F0.wireOp",EDGE,"E499"),sQuery(id+"F0.wireOp",EDGE,"E500"),sQuery(id+"F0.wireOp",EDGE,"E501"),sQuery(id+"F0.wireOp",EDGE,"E502"),sQuery(id+"F0.wireOp",EDGE,"E503"),sQuery(id+"F0.wireOp",EDGE,"E504"),sQuery(id+"F0.wireOp",EDGE,"E505"),sQuery(id+"F0.wireOp",EDGE,"E506"),sQuery(id+"F0.wireOp",EDGE,"E507"),sQuery(id+"F0.wireOp",EDGE,"E508"),sQuery(id+"F0.wireOp",EDGE,"E509"),sQuery(id+"F0.wireOp",EDGE,"E510"),sQuery(id+"F0.wireOp",EDGE,"E511"),sQuery(id+"F0.wireOp",EDGE,"E512"),sQuery(id+"F0.wireOp",EDGE,"E513"),sQuery(id+"F0.wireOp",EDGE,"E514"),sQuery(id+"F0.wireOp",EDGE,"E515"),sQuery(id+"F0.wireOp",EDGE,"E516"),sQuery(id+"F0.wireOp",EDGE,"E517"),sQuery(id+"F0.wireOp",EDGE,"E518"),sQuery(id+"F0.wireOp",EDGE,"E519"),sQuery(id+"F0.wireOp",EDGE,"E520"),sQuery(id+"F0.wireOp",EDGE,"E521"),sQuery(id+"F0.wireOp",EDGE,"E522"),sQuery(id+"F0.wireOp",EDGE,"E523"),sQuery(id+"F0.wireOp",EDGE,"E524"),sQuery(id+"F0.wireOp",EDGE,"E525"),sQuery(id+"F0.wireOp",EDGE,"E526"),sQuery(id+"F0.wireOp",EDGE,"E527"),sQuery(id+"F0.wireOp",EDGE,"E528"),sQuery(id+"F0.wireOp",EDGE,"E529"),sQuery(id+"F0.wireOp",EDGE,"E530"),sQuery(id+"F0.wireOp",EDGE,"E531"),sQuery(id+"F0.wireOp",EDGE,"E532"),sQuery(id+"F0.wireOp",EDGE,"E533"),sQuery(id+"F0.wireOp",EDGE,"E534"),sQuery(id+"F0.wireOp",EDGE,"E535"),sQuery(id+"F0.wireOp",EDGE,"E536"),sQuery(id+"F0.wireOp",EDGE,"E537"),sQuery(id+"F0.wireOp",EDGE,"E538"),sQuery(id+"F0.wireOp",EDGE,"E539"),sQuery(id+"F0.wireOp",EDGE,"E540"),sQuery(id+"F0.wireOp",EDGE,"E541"),sQuery(id+"F0.wireOp",EDGE,"E542"),sQuery(id+"F0.wireOp",EDGE,"E543"),sQuery(id+"F0.wireOp",EDGE,"E544"),sQuery(id+"F0.wireOp",EDGE,"E545"),sQuery(id+"F0.wireOp",EDGE,"E546"),sQuery(id+"F0.wireOp",EDGE,"E547"),sQuery(id+"F0.wireOp",EDGE,"E548"),sQuery(id+"F0.wireOp",EDGE,"E549"),sQuery(id+"F0.wireOp",EDGE,"E550"),sQuery(id+"F0.wireOp",EDGE,"E551"),sQuery(id+"F0.wireOp",EDGE,"E552"),sQuery(id+"F0.wireOp",EDGE,"E553"),sQuery(id+"F0.wireOp",EDGE,"E554"),sQuery(id+"F0.wireOp",EDGE,"E555"),sQuery(id+"F0.wireOp",EDGE,"E556"),sQuery(id+"F0.wireOp",EDGE,"E557"),sQuery(id+"F0.wireOp",EDGE,"E558"),sQuery(id+"F0.wireOp",EDGE,"E559"),sQuery(id+"F0.wireOp",EDGE,"E560"),sQuery(id+"F0.wireOp",EDGE,"E561"),sQuery(id+"F0.wireOp",EDGE,"E562"),sQuery(id+"F0.wireOp",EDGE,"E563"),sQuery(id+"F0.wireOp",EDGE,"E564"),sQuery(id+"F0.wireOp",EDGE,"E565"),sQuery(id+"F0.wireOp",EDGE,"E566"),sQuery(id+"F0.wireOp",EDGE,"E567"),sQuery(id+"F0.wireOp",EDGE,"E568"),sQuery(id+"F0.wireOp",EDGE,"E569"),sQuery(id+"F0.wireOp",EDGE,"E570"),sQuery(id+"F0.wireOp",EDGE,"E571"),sQuery(id+"F0.wireOp",EDGE,"E572"),sQuery(id+"F0.wireOp",EDGE,"E573"),sQuery(id+"F0.wireOp",EDGE,"E574"),sQuery(id+"F0.wireOp",EDGE,"E575"),sQuery(id+"F0.wireOp",EDGE,"E576"),sQuery(id+"F0.wireOp",EDGE,"E577"),sQuery(id+"F0.wireOp",EDGE,"E578"),sQuery(id+"F0.wireOp",EDGE,"E579"),sQuery(id+"F0.wireOp",EDGE,"E580"),sQuery(id+"F0.wireOp",EDGE,"E581"),sQuery(id+"F0.wireOp",EDGE,"E582"),sQuery(id+"F0.wireOp",EDGE,"E583"),sQuery(id+"F0.wireOp",EDGE,"E584"),sQuery(id+"F0.wireOp",EDGE,"E585"),sQuery(id+"F0.wireOp",EDGE,"E586"),sQuery(id+"F0.wireOp",EDGE,"E587"),sQuery(id+"F0.wireOp",EDGE,"E588"),sQuery(id+"F0.wireOp",EDGE,"E589"),sQuery(id+"F0.wireOp",EDGE,"E590"),sQuery(id+"F0.wireOp",EDGE,"E591"),sQuery(id+"F0.wireOp",EDGE,"E592"),sQuery(id+"F0.wireOp",EDGE,"E593"),sQuery(id+"F0.wireOp",EDGE,"E594"),sQuery(id+"F0.wireOp",EDGE,"E595"),sQuery(id+"F0.wireOp",EDGE,"E596"),sQuery(id+"F0.wireOp",EDGE,"E597"),sQuery(id+"F0.wireOp",EDGE,"E598"),sQuery(id+"F0.wireOp",EDGE,"E599"),sQuery(id+"F0.wireOp",EDGE,"E600"),sQuery(id+"F0.wireOp",EDGE,"E601"),sQuery(id+"F0.wireOp",EDGE,"E602"),sQuery(id+"F0.wireOp",EDGE,"E603"),sQuery(id+"F0.wireOp",EDGE,"E604"),sQuery(id+"F0.wireOp",EDGE,"E605"),sQuery(id+"F0.wireOp",EDGE,"E606"),sQuery(id+"F0.wireOp",EDGE,"E607"),sQuery(id+"F0.wireOp",EDGE,"E608"),sQuery(id+"F0.wireOp",EDGE,"E609"),sQuery(id+"F0.wireOp",EDGE,"E610"),sQuery(id+"F0.wireOp",EDGE,"E611"),sQuery(id+"F0.wireOp",EDGE,"E612"),sQuery(id+"F0.wireOp",EDGE,"E613"),sQuery(id+"F0.wireOp",EDGE,"E614"),sQuery(id+"F0.wireOp",EDGE,"E615"),sQuery(id+"F0.wireOp",EDGE,"E616"),sQuery(id+"F0.wireOp",EDGE,"E617"),sQuery(id+"F0.wireOp",EDGE,"E618"),sQuery(id+"F0.wireOp",EDGE,"E619"),sQuery(id+"F0.wireOp",EDGE,"E620"),sQuery(id+"F0.wireOp",EDGE,"E621"),sQuery(id+"F0.wireOp",EDGE,"E622"),sQuery(id+"F0.wireOp",EDGE,"E623"),sQuery(id+"F0.wireOp",EDGE,"E624"),sQuery(id+"F0.wireOp",EDGE,"E625"),sQuery(id+"F0.wireOp",EDGE,"E626"),sQuery(id+"F0.wireOp",EDGE,"E627"),sQuery(id+"F0.wireOp",EDGE,"E628"),sQuery(id+"F0.wireOp",EDGE,"E629"),sQuery(id+"F0.wireOp",EDGE,"E630"),sQuery(id+"F0.wireOp",EDGE,"E631"),sQuery(id+"F0.wireOp",EDGE,"E632"),sQuery(id+"F0.wireOp",EDGE,"E633"),sQuery(id+"F0.wireOp",EDGE,"E634"),sQuery(id+"F0.wireOp",EDGE,"E635"),sQuery(id+"F0.wireOp",EDGE,"E636"),sQuery(id+"F0.wireOp",EDGE,"E637"),sQuery(id+"F0.wireOp",EDGE,"E638"),sQuery(id+"F0.wireOp",EDGE,"E639"),sQuery(id+"F0.wireOp",EDGE,"E640"),sQuery(id+"F0.wireOp",EDGE,"E641"),sQuery(id+"F0.wireOp",EDGE,"E642"),sQuery(id+"F0.wireOp",EDGE,"E643"),sQuery(id+"F0.wireOp",EDGE,"E644"),sQuery(id+"F0.wireOp",EDGE,"E645"),sQuery(id+"F0.wireOp",EDGE,"E646"),sQuery(id+"F0.wireOp",EDGE,"E647"),sQuery(id+"F0.wireOp",EDGE,"E648"),sQuery(id+"F0.wireOp",EDGE,"E649"),sQuery(id+"F0.wireOp",EDGE,"E650"),sQuery(id+"F0.wireOp",EDGE,"E651"),sQuery(id+"F0.wireOp",EDGE,"E652"),sQuery(id+"F0.wireOp",EDGE,"E653"),sQuery(id+"F0.wireOp",EDGE,"E654"),sQuery(id+"F0.wireOp",EDGE,"E655"),sQuery(id+"F0.wireOp",EDGE,"E656"),sQuery(id+"F0.wireOp",EDGE,"E657"),sQuery(id+"F0.wireOp",EDGE,"E658"),sQuery(id+"F0.wireOp",EDGE,"E659"),sQuery(id+"F0.wireOp",EDGE,"E660"),sQuery(id+"F0.wireOp",EDGE,"E661"),sQuery(id+"F0.wireOp",EDGE,"E662"),sQuery(id+"F0.wireOp",EDGE,"E663"),sQuery(id+"F0.wireOp",EDGE,"E664"),sQuery(id+"F0.wireOp",EDGE,"E665"),sQuery(id+"F0.wireOp",EDGE,"E666"),sQuery(id+"F0.wireOp",EDGE,"E667"),sQuery(id+"F0.wireOp",EDGE,"E668"),sQuery(id+"F0.wireOp",EDGE,"E669"),sQuery(id+"F0.wireOp",EDGE,"E670"),sQuery(id+"F0.wireOp",EDGE,"E671"),sQuery(id+"F0.wireOp",EDGE,"E672"),sQuery(id+"F0.wireOp",EDGE,"E673"),sQuery(id+"F0.wireOp",EDGE,"E674"),sQuery(id+"F0.wireOp",EDGE,"E675"),sQuery(id+"F0.wireOp",EDGE,"E676"),sQuery(id+"F0.wireOp",EDGE,"E677"),sQuery(id+"F0.wireOp",EDGE,"E678"),sQuery(id+"F0.wireOp",EDGE,"E679"),sQuery(id+"F0.wireOp",EDGE,"E680"),sQuery(id+"F0.wireOp",EDGE,"E681"),sQuery(id+"F0.wireOp",EDGE,"E682"),sQuery(id+"F0.wireOp",EDGE,"E683"),sQuery(id+"F0.wireOp",EDGE,"E684"),sQuery(id+"F0.wireOp",EDGE,"E685"),sQuery(id+"F0.wireOp",EDGE,"E686"),sQuery(id+"F0.wireOp",EDGE,"E687"),sQuery(id+"F0.wireOp",EDGE,"E688"),sQuery(id+"F0.wireOp",EDGE,"E689"),sQuery(id+"F0.wireOp",EDGE,"E690"),sQuery(id+"F0.wireOp",EDGE,"E691"),sQuery(id+"F0.wireOp",EDGE,"E692"),sQuery(id+"F0.wireOp",EDGE,"E693"),sQuery(id+"F0.wireOp",EDGE,"E694"),sQuery(id+"F0.wireOp",EDGE,"E695"),sQuery(id+"F0.wireOp",EDGE,"E696"),sQuery(id+"F0.wireOp",EDGE,"E697"),sQuery(id+"F0.wireOp",EDGE,"E698"),sQuery(id+"F0.wireOp",EDGE,"E699"),sQuery(id+"F0.wireOp",EDGE,"E700"),sQuery(id+"F0.wireOp",EDGE,"E701"),sQuery(id+"F0.wireOp",EDGE,"E702"),sQuery(id+"F0.wireOp",EDGE,"E703"),sQuery(id+"F0.wireOp",EDGE,"E704"),sQuery(id+"F0.wireOp",EDGE,"E705"),sQuery(id+"F0.wireOp",EDGE,"E706"),sQuery(id+"F0.wireOp",EDGE,"E707"),sQuery(id+"F0.wireOp",EDGE,"E708"),sQuery(id+"F0.wireOp",EDGE,"E709"),sQuery(id+"F0.wireOp",EDGE,"E710"),sQuery(id+"F0.wireOp",EDGE,"E711"),sQuery(id+"F0.wireOp",EDGE,"E712"),sQuery(id+"F0.wireOp",EDGE,"E713"),sQuery(id+"F0.wireOp",EDGE,"E714"),sQuery(id+"F0.wireOp",EDGE,"E715"),sQuery(id+"F0.wireOp",EDGE,"E716"),sQuery(id+"F0.wireOp",EDGE,"E717"),sQuery(id+"F0.wireOp",EDGE,"E718"),sQuery(id+"F0.wireOp",EDGE,"E719"),sQuery(id+"F0.wireOp",EDGE,"E720"),sQuery(id+"F0.wireOp",EDGE,"E721"),sQuery(id+"F0.wireOp",EDGE,"E722"),sQuery(id+"F0.wireOp",EDGE,"E723"),sQuery(id+"F0.wireOp",EDGE,"E724"),sQuery(id+"F0.wireOp",EDGE,"E725"),sQuery(id+"F0.wireOp",EDGE,"E726"),sQuery(id+"F0.wireOp",EDGE,"E727"),sQuery(id+"F0.wireOp",EDGE,"E728"),sQuery(id+"F0.wireOp",EDGE,"E729"),sQuery(id+"F0.wireOp",EDGE,"E730"),sQuery(id+"F0.wireOp",EDGE,"E731"),sQuery(id+"F0.wireOp",EDGE,"E732"),sQuery(id+"F0.wireOp",EDGE,"E733"),sQuery(id+"F0.wireOp",EDGE,"E734"),sQuery(id+"F0.wireOp",EDGE,"E735"),sQuery(id+"F0.wireOp",EDGE,"E736"),sQuery(id+"F0.wireOp",EDGE,"E737"),sQuery(id+"F0.wireOp",EDGE,"E738"),sQuery(id+"F0.wireOp",EDGE,"E739"),sQuery(id+"F0.wireOp",EDGE,"E740"),sQuery(id+"F0.wireOp",EDGE,"E741"),sQuery(id+"F0.wireOp",EDGE,"E742"),sQuery(id+"F0.wireOp",EDGE,"E743"),sQuery(id+"F0.wireOp",EDGE,"E744"),sQuery(id+"F0.wireOp",EDGE,"E745"),sQuery(id+"F0.wireOp",EDGE,"E746"),sQuery(id+"F0.wireOp",EDGE,"E747"),sQuery(id+"F0.wireOp",EDGE,"E748"),sQuery(id+"F0.wireOp",EDGE,"E749"),sQuery(id+"F0.wireOp",EDGE,"E750"),sQuery(id+"F0.wireOp",EDGE,"E751"),sQuery(id+"F0.wireOp",EDGE,"E752"),sQuery(id+"F0.wireOp",EDGE,"E753"),sQuery(id+"F0.wireOp",EDGE,"E754"),sQuery(id+"F0.wireOp",EDGE,"E755"),sQuery(id+"F0.wireOp",EDGE,"E756"),sQuery(id+"F0.wireOp",EDGE,"E757"),sQuery(id+"F0.wireOp",EDGE,"E758"),sQuery(id+"F0.wireOp",EDGE,"E759"),sQuery(id+"F0.wireOp",EDGE,"E760"),sQuery(id+"F0.wireOp",EDGE,"E761"),sQuery(id+"F0.wireOp",EDGE,"E762"),sQuery(id+"F0.wireOp",EDGE,"E763"),sQuery(id+"F0.wireOp",EDGE,"E764"),sQuery(id+"F0.wireOp",EDGE,"E765"),sQuery(id+"F0.wireOp",EDGE,"E766"),sQuery(id+"F0.wireOp",EDGE,"E767"),sQuery(id+"F0.wireOp",EDGE,"E768"),sQuery(id+"F0.wireOp",EDGE,"E769"),sQuery(id+"F0.wireOp",EDGE,"E770"),sQuery(id+"F0.wireOp",EDGE,"E771"),sQuery(id+"F0.wireOp",EDGE,"E772"),sQuery(id+"F0.wireOp",EDGE,"E773"),sQuery(id+"F0.wireOp",EDGE,"E774"),sQuery(id+"F0.wireOp",EDGE,"E775"),sQuery(id+"F0.wireOp",EDGE,"E776"),sQuery(id+"F0.wireOp",EDGE,"E777"),sQuery(id+"F0.wireOp",EDGE,"E778"),sQuery(id+"F0.wireOp",EDGE,"E779"),sQuery(id+"F0.wireOp",EDGE,"E780"),sQuery(id+"F0.wireOp",EDGE,"E781"),sQuery(id+"F0.wireOp",EDGE,"E782"),sQuery(id+"F0.wireOp",EDGE,"E783"),sQuery(id+"F0.wireOp",EDGE,"E784"),sQuery(id+"F0.wireOp",EDGE,"E785"),sQuery(id+"F0.wireOp",EDGE,"E786"),sQuery(id+"F0.wireOp",EDGE,"E787"),sQuery(id+"F0.wireOp",EDGE,"E788"),sQuery(id+"F0.wireOp",EDGE,"E789"),sQuery(id+"F0.wireOp",EDGE,"E790"),sQuery(id+"F0.wireOp",EDGE,"E791"),sQuery(id+"F0.wireOp",EDGE,"E792"),sQuery(id+"F0.wireOp",EDGE,"E793"),sQuery(id+"F0.wireOp",EDGE,"E794"),sQuery(id+"F0.wireOp",EDGE,"E795"),sQuery(id+"F0.wireOp",EDGE,"E796"),sQuery(id+"F0.wireOp",EDGE,"E797"),sQuery(id+"F0.wireOp",EDGE,"E798"),sQuery(id+"F0.wireOp",EDGE,"E799"),sQuery(id+"F0.wireOp",EDGE,"E800"),sQuery(id+"F0.wireOp",EDGE,"E801"),sQuery(id+"F0.wireOp",EDGE,"E802"),sQuery(id+"F0.wireOp",EDGE,"E803"),sQuery(id+"F0.wireOp",EDGE,"E804"),sQuery(id+"F0.wireOp",EDGE,"E805"),sQuery(id+"F0.wireOp",EDGE,"E806"),sQuery(id+"F0.wireOp",EDGE,"E807"),sQuery(id+"F0.wireOp",EDGE,"E808"),sQuery(id+"F0.wireOp",EDGE,"E809"),sQuery(id+"F0.wireOp",EDGE,"E810"),sQuery(id+"F0.wireOp",EDGE,"E811"),sQuery(id+"F0.wireOp",EDGE,"E812"),sQuery(id+"F0.wireOp",EDGE,"E813"),sQuery(id+"F0.wireOp",EDGE,"E814"),sQuery(id+"F0.wireOp",EDGE,"E815"),sQuery(id+"F0.wireOp",EDGE,"E816"),sQuery(id+"F0.wireOp",EDGE,"E817"),sQuery(id+"F0.wireOp",EDGE,"E818"),sQuery(id+"F0.wireOp",EDGE,"E819"),sQuery(id+"F0.wireOp",EDGE,"E820"),sQuery(id+"F0.wireOp",EDGE,"E821"),sQuery(id+"F0.wireOp",EDGE,"E822"),sQuery(id+"F0.wireOp",EDGE,"E823"),sQuery(id+"F0.wireOp",EDGE,"E824"),sQuery(id+"F0.wireOp",EDGE,"E825"),sQuery(id+"F0.wireOp",EDGE,"E826"),sQuery(id+"F0.wireOp",EDGE,"E827"),sQuery(id+"F0.wireOp",EDGE,"E828"),sQuery(id+"F0.wireOp",EDGE,"E829"),sQuery(id+"F0.wireOp",EDGE,"E830"),sQuery(id+"F0.wireOp",EDGE,"E831"),sQuery(id+"F0.wireOp",EDGE,"E832")])],"isStart":false});
            var sketch = newSketch(context, id + "F2", { "sketchPlane" : qUnion([Q0])});
            skCircle(sketch, "E834", {"center": v(-2.9, 0) * mm, "radius": 6 * mm});
            skCircle(sketch, "E835", {"center": v(-2.9, 0) * mm, "radius": 2.65 * mm});
            skSolve(sketch);
        }
        {
            var Q0;
            Q0=makeQuery(id+"F2.imprint","IMPRINT",FACE,{"disambiguationData":[TD([[makeQuery(id+"F2.imprint","IMPRINT",EDGE,{"derivedFrom":sQuery(id+"F2.wireOp",EDGE,"E834")}),1.0]])]});
            extrude(context, id + "F3", {"entities" : qUnion([Q0]), "operationType" : NewBodyOperationType.ADD, "depth" : 1 * mm});
        }
        {
            var Q0;
            Q0=makeQuery(id+"F3.opExtrude","CAP_EDGE",EDGE,{"disambiguationData":[OSD([sQuery(id+"F2.wireOp",EDGE,"E834")])],"isStart":false});
            fillet(context, id + "F4", {"entities" : qUnion([Q0]), "radius" : 0.4 * mm, "tangentPropagation" : true, "allowEdgeOverflow" : false});
        }
    });
